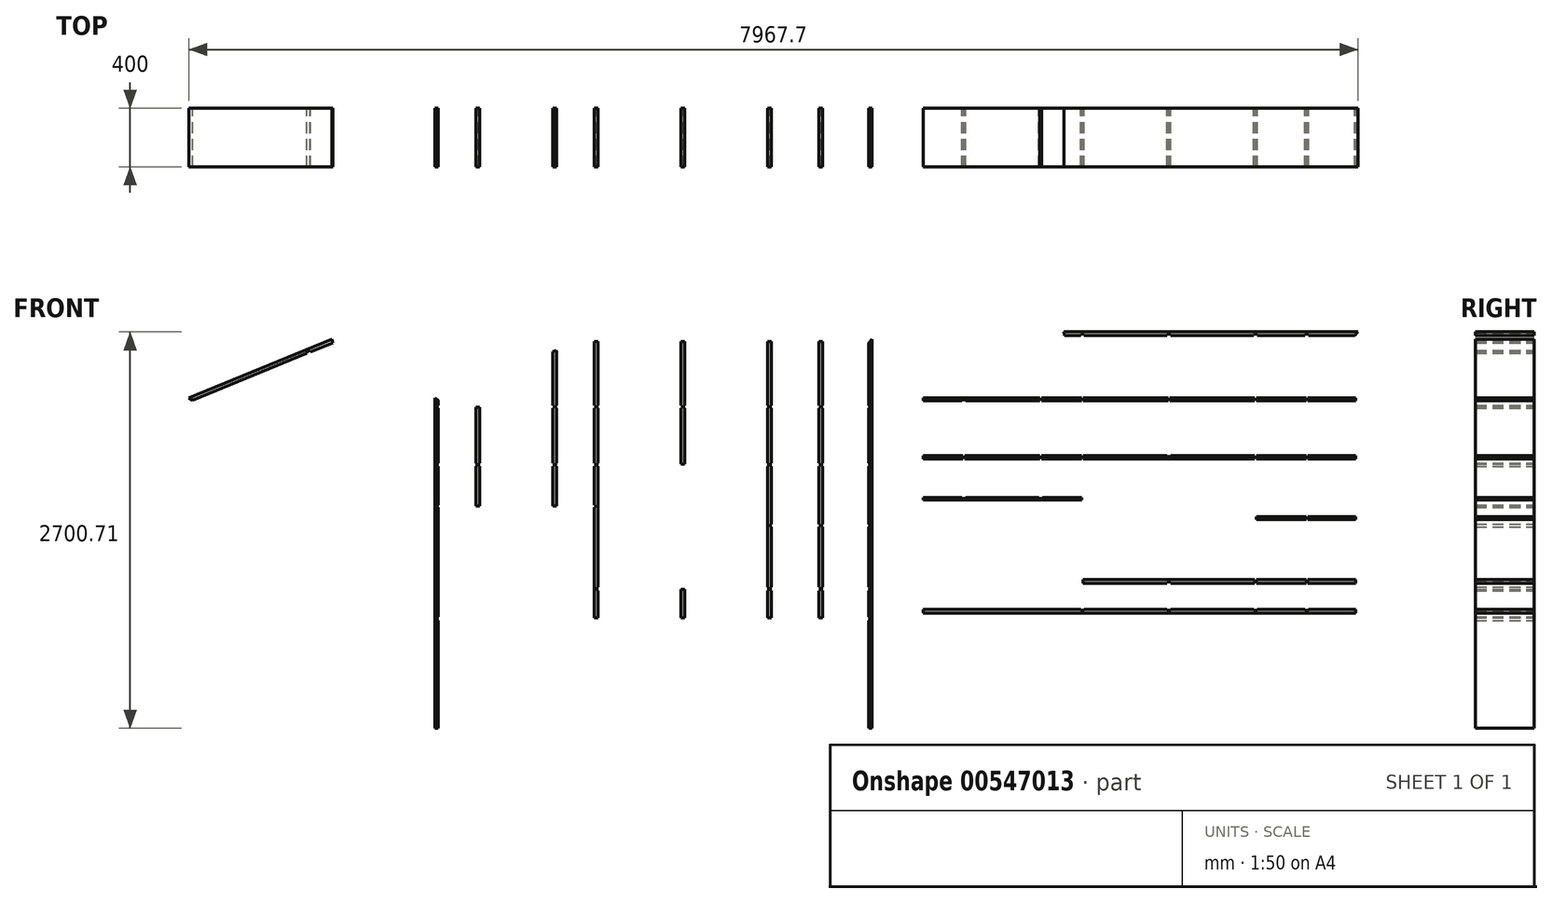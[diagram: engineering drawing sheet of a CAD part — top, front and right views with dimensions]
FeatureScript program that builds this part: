
annotation { "Feature Type Name" : "Feature", "Feature Type Description" : "" }
export const myFeature = defineFeature(function(context is Context, id is Id, definition is map)
    precondition{}
    {
        {
            var Q0;
            Q0=qCreatedBy(makeId("Front.planeOp"),FACE);
            var sketch = newSketch(context, id + "F0", { "sketchPlane" : qUnion([Q0])});
            skLineSegment(sketch, "E0", {"start": v(0, 0) * mm, "end": v(0, 2251) * mm});
            skLineSegment(sketch, "E1", {"start": v(0, 2251) * mm, "end": v(975, 2650) * mm});
            skLineSegment(sketch, "E2", {"start": v(975, 2650) * mm, "end": v(3933.36, 2650) * mm});
            skLineSegment(sketch, "E3", {"start": v(3933.36, 2650) * mm, "end": v(4900, 2240) * mm});
            skLineSegment(sketch, "E4", {"start": v(4900, 2240) * mm, "end": v(4900, 0) * mm});
            skLineSegment(sketch, "E5", {"start": v(4900, 0) * mm, "end": v(0, 0) * mm});
            skLineSegment(sketch, "E6", {"start": v(4550, 0) * mm, "end": v(4550, 2100) * mm});
            skLineSegment(sketch, "E7", {"start": v(4550, 2100) * mm, "end": v(3350, 2100) * mm});
            skLineSegment(sketch, "E8", {"start": v(3350, 2100) * mm, "end": v(3350, 0) * mm});
            skLineSegment(sketch, "E9.bottom", {"start": v(1200, 1695) * mm, "end": v(2180, 1695) * mm});
            skLineSegment(sketch, "E9.top", {"start": v(1200, 1050) * mm, "end": v(2180, 1050) * mm});
            skLineSegment(sketch, "E9.left", {"start": v(1200, 1695) * mm, "end": v(1200, 1050) * mm});
            skLineSegment(sketch, "E9.right", {"start": v(2180, 1695) * mm, "end": v(2180, 1050) * mm});
            skLineSegment(sketch, "E10", {"start": v(2980, 2650) * mm, "end": v(2980, 0) * mm});
            skLineSegment(sketch, "E11.0", {"start": v(24, 0) * mm, "end": v(24, 502) * mm});
            skLineSegment(sketch, "E12.0", {"start": v(2642, 2636) * mm, "end": v(2642, 2626) * mm});
            skLineSegment(sketch, "E13.0", {"start": v(2291.97, 1807) * mm, "end": v(2291.97, 2181) * mm});
            skLineSegment(sketch, "E14.0", {"start": v(2268, 1807) * mm, "end": v(2268, 2181) * mm});
            skLineSegment(sketch, "E15.0", {"start": v(2268, 1783) * mm, "end": v(2268, 962) * mm});
            skLineSegment(sketch, "E16.0", {"start": v(2292, 1783) * mm, "end": v(2292, 1390.5) * mm});
            skLineSegment(sketch, "E17.0", {"start": v(2292, 938) * mm, "end": v(2292, 752) * mm});
            skLineSegment(sketch, "E18.0", {"start": v(2268, 938) * mm, "end": v(2268, 752) * mm});
            skLineSegment(sketch, "E19.0", {"start": v(1702, 1800) * mm, "end": v(1702, 2181) * mm});
            skLineSegment(sketch, "E20.0", {"start": v(1678, 1800) * mm, "end": v(1678, 2181) * mm});
            skLineSegment(sketch, "E21.0", {"start": v(1112, 1807) * mm, "end": v(1112, 2181) * mm});
            skLineSegment(sketch, "E22.0", {"start": v(1088, 1807) * mm, "end": v(1088, 2181) * mm});
            skLineSegment(sketch, "E23.0", {"start": v(1088, 1783) * mm, "end": v(1088, 1522.2) * mm});
            skLineSegment(sketch, "E24.0", {"start": v(1112, 1783) * mm, "end": v(1112, 1222.6) * mm});
            skLineSegment(sketch, "E25.0", {"start": v(1088, 938) * mm, "end": v(1088, 752) * mm});
            skLineSegment(sketch, "E26.0", {"start": v(1112, 938) * mm, "end": v(1112, 752) * mm});
            skLineSegment(sketch, "E27.0", {"start": v(1105, 1783) * mm, "end": v(2275, 1783) * mm});
            skLineSegment(sketch, "E28.0", {"start": v(1105, 1807) * mm, "end": v(1678, 1807) * mm});
            skLineSegment(sketch, "E29.0", {"start": v(1105, 938) * mm, "end": v(1678, 938) * mm});
            skLineSegment(sketch, "E30.0", {"start": v(1105, 962) * mm, "end": v(2275, 962) * mm});
            skLineSegment(sketch, "E31.0", {"start": v(1095, 1807) * mm, "end": v(821.64, 1807) * mm});
            skLineSegment(sketch, "E32.0", {"start": v(1095, 1783) * mm, "end": v(821.64, 1783) * mm});
            skLineSegment(sketch, "E33.0", {"start": v(2284.97, 938) * mm, "end": v(2625, 938) * mm});
            skLineSegment(sketch, "E34.0", {"start": v(2284.97, 962) * mm, "end": v(2625, 962) * mm});
            skLineSegment(sketch, "E35.0", {"start": v(2284.97, 1783) * mm, "end": v(2625, 1783) * mm});
            skLineSegment(sketch, "E36.0", {"start": v(2284.97, 1807) * mm, "end": v(2625, 1807) * mm});
            skLineSegment(sketch, "E37.0", {"start": v(1678, 945) * mm, "end": v(1678, 752) * mm});
            skLineSegment(sketch, "E38.0", {"start": v(1702, 945) * mm, "end": v(1702, 752) * mm});
            skLineSegment(sketch, "E39.0", {"start": v(1095, 1522.2) * mm, "end": v(828.64, 1522.2) * mm});
            skLineSegment(sketch, "E40.0", {"start": v(1095, 1504.2) * mm, "end": v(1088, 1504.2) * mm});
            skLineSegment(sketch, "E41.0", {"start": v(2963, 759) * mm, "end": v(2642, 759) * mm});
            skLineSegment(sketch, "E42", {"start": v(1112, 1222.6) * mm, "end": v(1112, 962) * mm});
            skLineSegment(sketch, "E43.bottom", {"start": v(100, 0) * mm, "end": v(500, 0) * mm});
            skLineSegment(sketch, "E43.left", {"start": v(100, 0) * mm, "end": v(100, 450) * mm});
            skLineSegment(sketch, "E43.right", {"start": v(500, 0) * mm, "end": v(500, 450) * mm});
            skLineSegment(sketch, "E44.bottom", {"start": v(576, 0) * mm, "end": v(976, 0) * mm});
            skLineSegment(sketch, "E44.left", {"start": v(576, 0) * mm, "end": v(576, 450) * mm});
            skLineSegment(sketch, "E44.right", {"start": v(976, 0) * mm, "end": v(976, 450) * mm});
            skLineSegment(sketch, "E45.bottom", {"start": v(1052, 0) * mm, "end": v(1452, 0) * mm});
            skLineSegment(sketch, "E45.left", {"start": v(1052, 0) * mm, "end": v(1052, 650) * mm});
            skLineSegment(sketch, "E45.right", {"start": v(1452, 0) * mm, "end": v(1452, 650) * mm});
            skLineSegment(sketch, "E46.bottom", {"start": v(1528, 0) * mm, "end": v(1928, 0) * mm});
            skLineSegment(sketch, "E46.left", {"start": v(1528, 0) * mm, "end": v(1528, 650) * mm});
            skLineSegment(sketch, "E46.right", {"start": v(1928, 0) * mm, "end": v(1928, 650) * mm});
            skLineSegment(sketch, "E47.bottom", {"start": v(2004, -2.2) * mm, "end": v(2404, -2.2) * mm});
            skLineSegment(sketch, "E47.left", {"start": v(2004, 447.8) * mm, "end": v(2004, 650) * mm});
            skLineSegment(sketch, "E47.right", {"start": v(2404, 447.8) * mm, "end": v(2404, 650) * mm});
            skLineSegment(sketch, "E48.bottom", {"start": v(2450, 0) * mm, "end": v(2850, 0) * mm});
            skLineSegment(sketch, "E49.bottom", {"start": v(2480, 0) * mm, "end": v(2880, 0) * mm});
            skLineSegment(sketch, "E49.left", {"start": v(2480, 0) * mm, "end": v(2480, 650) * mm});
            skLineSegment(sketch, "E49.right", {"start": v(2880, 0) * mm, "end": v(2880, 650) * mm});
            skLineSegment(sketch, "E50", {"start": v(2642, 2636) * mm, "end": v(2618, 2636) * mm});
            skLineSegment(sketch, "E51.trimOffspring", {"start": v(2642, 2626) * mm, "end": v(2956, 2626) * mm});
            skLineSegment(sketch, "E52.trimOffspring", {"start": v(2956, 2249) * mm, "end": v(2956, 2199) * mm});
            skLineSegment(sketch, "E53.trimOffspring", {"start": v(2618, 2249) * mm, "end": v(2618, 2199) * mm});
            skLineSegment(sketch, "E54.trimOffspring", {"start": v(2642, 2249) * mm, "end": v(2642, 2199) * mm});
            skLineSegment(sketch, "E55", {"start": v(1112, 2636) * mm, "end": v(1088, 2636) * mm});
            skLineSegment(sketch, "E56.trimOffspring", {"start": v(1112, 2626) * mm, "end": v(1678, 2626) * mm});
            skLineSegment(sketch, "E57", {"start": v(1702, 2636) * mm, "end": v(1678, 2636) * mm});
            skLineSegment(sketch, "E58.trimOffspring", {"start": v(1702, 2626) * mm, "end": v(2268, 2626) * mm});
            skLineSegment(sketch, "E59", {"start": v(2291.97, 2636) * mm, "end": v(2268, 2636) * mm});
            skLineSegment(sketch, "E60.trimOffspring", {"start": v(2291.97, 2626) * mm, "end": v(2618, 2626) * mm});
            skLineSegment(sketch, "E61", {"start": v(17, 1807) * mm, "end": v(17, 1783) * mm});
            skLineSegment(sketch, "E62.trimOffspring", {"start": v(24, 759) * mm, "end": v(24, 1504.2) * mm});
            skLineSegment(sketch, "E63.trimOffspring", {"start": v(17, 1522.2) * mm, "end": v(17, 1504.2) * mm});
            skLineSegment(sketch, "E64.trimOffspring", {"start": v(24, 1522.2) * mm, "end": v(24, 1783) * mm});
            skLineSegment(sketch, "E65.trimOffspring", {"start": v(24, 1807) * mm, "end": v(24, 2181) * mm});
            skLineSegment(sketch, "E66.trimOffspring", {"start": v(24, 502) * mm, "end": v(24, 735) * mm});
            skLineSegment(sketch, "E67", {"start": v(2963, 1807) * mm, "end": v(2963, 1783) * mm});
            skLineSegment(sketch, "E68.trimOffspring", {"start": v(2963, 1390.5) * mm, "end": v(2963, 1372.5) * mm});
            skLineSegment(sketch, "E69.trimOffspring", {"start": v(2956, 938) * mm, "end": v(2956, 759) * mm});
            skLineSegment(sketch, "E70.trimOffspring", {"start": v(2956, 1783) * mm, "end": v(2956, 1390.5) * mm});
            skLineSegment(sketch, "E71.trimOffspring", {"start": v(2818.11, 1783) * mm, "end": v(2963, 1783) * mm});
            skLineSegment(sketch, "E72", {"start": v(2635, 1807) * mm, "end": v(2635, 1783) * mm});
            skLineSegment(sketch, "E73.trimOffspring", {"start": v(2635, 938) * mm, "end": v(2963, 938) * mm});
            skLineSegment(sketch, "E74.trimOffspring", {"start": v(2642, 938) * mm, "end": v(2642, 752) * mm});
            skLineSegment(sketch, "E75.trimOffspring", {"start": v(2635, 962) * mm, "end": v(2818.11, 962) * mm});
            skLineSegment(sketch, "E76.trimOffspring", {"start": v(2635, 1390.5) * mm, "end": v(2635, 1372.5) * mm});
            skLineSegment(sketch, "E77.trimOffspring", {"start": v(2635, 1807) * mm, "end": v(2963, 1807) * mm});
            skLineSegment(sketch, "E78.trimOffspring", {"start": v(2635, 1783) * mm, "end": v(2818.11, 1783) * mm});
            skLineSegment(sketch, "E79.trimOffspring", {"start": v(2642, 1783) * mm, "end": v(2642, 1390.5) * mm});
            skLineSegment(sketch, "E80", {"start": v(2625, 1807) * mm, "end": v(2625, 1783) * mm});
            skLineSegment(sketch, "E81.trimOffspring", {"start": v(2625, 1390.5) * mm, "end": v(2625, 1372.5) * mm});
            skLineSegment(sketch, "E82.trimOffspring", {"start": v(2618, 1783) * mm, "end": v(2618, 1390.5) * mm});
            skLineSegment(sketch, "E83.trimOffspring", {"start": v(2618, 938) * mm, "end": v(2618, 752) * mm});
            skLineSegment(sketch, "E84.trimOffspring", {"start": v(2818.11, 962) * mm, "end": v(2963, 962) * mm});
            skLineSegment(sketch, "E85", {"start": v(1702, 1800) * mm, "end": v(1678, 1800) * mm});
            skLineSegment(sketch, "E86.trimOffspring", {"start": v(1702, 1807) * mm, "end": v(2275, 1807) * mm});
            skLineSegment(sketch, "E87.trimOffspring", {"start": v(2284.97, 1807) * mm, "end": v(2284.97, 1783) * mm});
            skLineSegment(sketch, "E88.trimOffspring", {"start": v(2284.97, 1390.5) * mm, "end": v(2284.97, 1372.5) * mm});
            skLineSegment(sketch, "E89.trimOffspring", {"start": v(2275, 1783) * mm, "end": v(2275, 1807) * mm});
            skLineSegment(sketch, "E90.trimOffspring", {"start": v(2275, 938) * mm, "end": v(2275, 962) * mm});
            skLineSegment(sketch, "E91.trimOffspring", {"start": v(2956, 502) * mm, "end": v(2956, 0) * mm});
            skLineSegment(sketch, "E92.trimOffspring", {"start": v(1678, 759) * mm, "end": v(1112, 759) * mm});
            skLineSegment(sketch, "E93", {"start": v(1702, 945) * mm, "end": v(1678, 945) * mm});
            skLineSegment(sketch, "E94.trimOffspring", {"start": v(1702, 938) * mm, "end": v(2275, 938) * mm});
            skLineSegment(sketch, "E95.trimOffspring", {"start": v(287.5, 1807) * mm, "end": v(287.5, 1783) * mm});
            skLineSegment(sketch, "E96.trimOffspring", {"start": v(287.5, 1807) * mm, "end": v(17, 1807) * mm});
            skLineSegment(sketch, "E97.trimOffspring", {"start": v(280.5, 1807) * mm, "end": v(280.5, 2188) * mm});
            skLineSegment(sketch, "E98.trimOffspring", {"start": v(304.5, 1807) * mm, "end": v(304.5, 2188) * mm});
            skLineSegment(sketch, "E99.trimOffspring", {"start": v(287.5, 1783) * mm, "end": v(17, 1783) * mm});
            skLineSegment(sketch, "E100.trimOffspring", {"start": v(297.5, 1783) * mm, "end": v(297.5, 1807) * mm});
            skLineSegment(sketch, "E101.trimOffspring", {"start": v(280.5, 1522.2) * mm, "end": v(17, 1522.2) * mm});
            skLineSegment(sketch, "E102.trimOffspring", {"start": v(24, 1504.2) * mm, "end": v(17, 1504.2) * mm});
            skLineSegment(sketch, "E103.trimOffspring", {"start": v(304.5, 1515.2) * mm, "end": v(304.5, 1783) * mm});
            skLineSegment(sketch, "E104.trimOffspring", {"start": v(828.64, 2564.17) * mm, "end": v(828.64, 2249) * mm});
            skLineSegment(sketch, "E105.trimOffspring", {"start": v(804.64, 2565.16) * mm, "end": v(804.64, 2249) * mm});
            skLineSegment(sketch, "E106.trimOffspring", {"start": v(804.64, 1783) * mm, "end": v(804.64, 1515.2) * mm});
            skLineSegment(sketch, "E107.trimOffspring", {"start": v(828.64, 1783) * mm, "end": v(828.64, 1515.2) * mm});
            skLineSegment(sketch, "E108.trimOffspring", {"start": v(811.64, 1783) * mm, "end": v(297.5, 1783) * mm});
            skLineSegment(sketch, "E109.trimOffspring", {"start": v(811.64, 1807) * mm, "end": v(297.5, 1807) * mm});
            skLineSegment(sketch, "E110", {"start": v(1105, 1807) * mm, "end": v(1105, 1783) * mm});
            skLineSegment(sketch, "E111.trimOffspring", {"start": v(1095, 1807) * mm, "end": v(1095, 1783) * mm});
            skLineSegment(sketch, "E112.trimOffspring", {"start": v(1095, 1522.2) * mm, "end": v(1095, 1504.2) * mm});
            skLineSegment(sketch, "E113.trimOffspring", {"start": v(1088, 1504.2) * mm, "end": v(1088, 1222.6) * mm});
            skLineSegment(sketch, "E114.trimOffspring", {"start": v(1088, 1222.6) * mm, "end": v(1088, 938) * mm});
            skLineSegment(sketch, "E115", {"start": v(1105, 962) * mm, "end": v(1105, 938) * mm});
            skLineSegment(sketch, "E116.trimOffspring", {"start": v(280.5, 1515.2) * mm, "end": v(280.5, 1783) * mm});
            skLineSegment(sketch, "E117", {"start": v(304.5, 1522.2) * mm, "end": v(804.64, 1522.2) * mm});
            skLineSegment(sketch, "E118.0", {"start": v(576, 650) * mm, "end": v(976, 650) * mm});
            skLineSegment(sketch, "E119.0", {"start": v(100, 650) * mm, "end": v(500, 650) * mm});
            skLineSegment(sketch, "E120", {"start": v(500, 650) * mm, "end": v(500, 450) * mm});
            skLineSegment(sketch, "E121", {"start": v(100, 650) * mm, "end": v(100, 450) * mm});
            skLineSegment(sketch, "E122", {"start": v(576, 650) * mm, "end": v(576, 450) * mm});
            skLineSegment(sketch, "E123", {"start": v(976, 650) * mm, "end": v(976, 450) * mm});
            skLineSegment(sketch, "E124", {"start": v(2284.97, 1372.5) * mm, "end": v(2625, 1372.5) * mm});
            skLineSegment(sketch, "E125.0", {"start": v(2284.97, 1390.5) * mm, "end": v(2625, 1390.5) * mm});
            skPoint(sketch, "E126.orphan", {"position": v(2292, 1372.5) * mm});
            skLineSegment(sketch, "E127.trimOffspring", {"start": v(2292, 1372.5) * mm, "end": v(2292, 962) * mm});
            skLineSegment(sketch, "E128.trimOffspring", {"start": v(2284.97, 962) * mm, "end": v(2284.97, 938) * mm});
            skPoint(sketch, "E129.orphan", {"position": v(2956, 1372.5) * mm});
            skLineSegment(sketch, "E130.trimOffspring", {"start": v(2956, 1372.5) * mm, "end": v(2956, 962) * mm});
            skLineSegment(sketch, "E131.trimOffspring", {"start": v(2963, 962) * mm, "end": v(2963, 938) * mm});
            skLineSegment(sketch, "E132", {"start": v(2625, 962) * mm, "end": v(2625, 938) * mm});
            skLineSegment(sketch, "E133", {"start": v(2635, 962) * mm, "end": v(2635, 938) * mm});
            skLineSegment(sketch, "E134.trimOffspring", {"start": v(2642, 1372.5) * mm, "end": v(2642, 962) * mm});
            skLineSegment(sketch, "E135.trimOffspring", {"start": v(2618, 1372.5) * mm, "end": v(2618, 962) * mm});
            skLineSegment(sketch, "E136.trimOffspring", {"start": v(2635, 1372.5) * mm, "end": v(2963, 1372.5) * mm});
            skLineSegment(sketch, "E137.trimOffspring", {"start": v(2635, 1390.5) * mm, "end": v(2963, 1390.5) * mm});
            skLineSegment(sketch, "E138.trimOffspring", {"start": v(804.64, 2249) * mm, "end": v(804.64, 2199) * mm});
            skLineSegment(sketch, "E139.trimOffspring", {"start": v(828.64, 2249) * mm, "end": v(828.64, 2199) * mm});
            skLineSegment(sketch, "E140.trimOffspring", {"start": v(828.64, 2564.17) * mm, "end": v(979.72, 2626) * mm});
            skLineSegment(sketch, "E141.trimOffspring", {"start": v(804.64, 2565.16) * mm, "end": v(824.85, 2573.43) * mm});
            skLineSegment(sketch, "E142", {"start": v(1088, 2636) * mm, "end": v(1088, 2249) * mm});
            skLineSegment(sketch, "E143", {"start": v(1112, 2636) * mm, "end": v(1112, 2249) * mm});
            skLineSegment(sketch, "E144", {"start": v(1678, 2249) * mm, "end": v(1678, 2636) * mm});
            skLineSegment(sketch, "E145", {"start": v(1702, 2636) * mm, "end": v(1702, 2249) * mm});
            skLineSegment(sketch, "E146", {"start": v(2268, 2636) * mm, "end": v(2268, 2249) * mm});
            skLineSegment(sketch, "E147", {"start": v(2291.97, 2249) * mm, "end": v(2291.97, 2636) * mm});
            skLineSegment(sketch, "E148", {"start": v(2618, 2636) * mm, "end": v(2618, 2249) * mm});
            skLineSegment(sketch, "E149", {"start": v(2642, 2626) * mm, "end": v(2642, 2249) * mm});
            skLineSegment(sketch, "E150", {"start": v(2956, 2626) * mm, "end": v(2956, 2249) * mm});
            skLineSegment(sketch, "E151.trimOffspring", {"start": v(1088, 759) * mm, "end": v(17, 759) * mm});
            skLineSegment(sketch, "E152.0", {"start": v(280.5, 1515.2) * mm, "end": v(304.5, 1515.2) * mm});
            skLineSegment(sketch, "E153.trimOffspring", {"start": v(804.64, 1515.2) * mm, "end": v(828.64, 1515.2) * mm});
            skLineSegment(sketch, "E154", {"start": v(1088, 1504.2) * mm, "end": v(24, 1504.2) * mm});
            skLineSegment(sketch, "E155.trimOffspring", {"start": v(2956, 526) * mm, "end": v(2956, 502) * mm});
            skLineSegment(sketch, "E156", {"start": v(2004, 447.8) * mm, "end": v(2004, -2.2) * mm});
            skLineSegment(sketch, "E157", {"start": v(2404, 447.8) * mm, "end": v(2404, -2.2) * mm});
            skLineSegment(sketch, "E158.trimOffspring", {"start": v(1052, 650) * mm, "end": v(1452, 650) * mm});
            skLineSegment(sketch, "E159.trimOffspring", {"start": v(1528, 650) * mm, "end": v(1928, 650) * mm});
            skLineSegment(sketch, "E160.trimOffspring", {"start": v(2004, 650) * mm, "end": v(2404, 650) * mm});
            skLineSegment(sketch, "E161.trimOffspring", {"start": v(2480, 650) * mm, "end": v(2880, 650) * mm});
            skLineSegment(sketch, "E162", {"start": v(1685, 741) * mm, "end": v(1695, 741) * mm});
            skLineSegment(sketch, "E163", {"start": v(2956, 550) * mm, "end": v(2956, 526) * mm});
            skLineSegment(sketch, "E164.0", {"start": v(2642, 752) * mm, "end": v(2618, 752) * mm});
            skLineSegment(sketch, "E165.trimOffspring", {"start": v(2618, 759) * mm, "end": v(2292, 759) * mm});
            skLineSegment(sketch, "E166.trimOffspring", {"start": v(2268, 759) * mm, "end": v(1702, 759) * mm});
            skLineSegment(sketch, "E167.trimOffspring", {"start": v(2292, 752) * mm, "end": v(2268, 752) * mm});
            skLineSegment(sketch, "E168.trimOffspring", {"start": v(1112, 752) * mm, "end": v(1088, 752) * mm});
            skLineSegment(sketch, "E169.trimOffspring", {"start": v(1702, 752) * mm, "end": v(1678, 752) * mm});
            skLineSegment(sketch, "E170.trimOffspring", {"start": v(2963, 759) * mm, "end": v(2963, 735) * mm});
            skLineSegment(sketch, "E171.trimOffspring", {"start": v(2956, 735) * mm, "end": v(2956, 550) * mm});
            skLineSegment(sketch, "E172", {"start": v(975, 2650) * mm, "end": v(979.72, 2626) * mm});
            skLineSegment(sketch, "E173", {"start": v(17, 2199) * mm, "end": v(17, 2181) * mm});
            skLineSegment(sketch, "E174", {"start": v(17, 2181) * mm, "end": v(24, 2181) * mm});
            skLineSegment(sketch, "E175.0", {"start": v(17, 2181) * mm, "end": v(280.5, 2181) * mm});
            skLineSegment(sketch, "E176.0", {"start": v(17, 2199) * mm, "end": v(298.67, 2199) * mm});
            skLineSegment(sketch, "E177", {"start": v(2963, 2199) * mm, "end": v(2963, 2181) * mm});
            skLineSegment(sketch, "E178", {"start": v(2635, 2199) * mm, "end": v(2635, 2181) * mm});
            skLineSegment(sketch, "E179", {"start": v(2625, 2199) * mm, "end": v(2625, 2181) * mm});
            skLineSegment(sketch, "E180.trimOffspring", {"start": v(2635, 2199) * mm, "end": v(2963, 2199) * mm});
            skLineSegment(sketch, "E181.trimOffspring", {"start": v(2635, 2181) * mm, "end": v(2963, 2181) * mm});
            skLineSegment(sketch, "E182.trimOffspring", {"start": v(2284.97, 2199) * mm, "end": v(2284.97, 2181) * mm});
            skLineSegment(sketch, "E183.trimOffspring", {"start": v(2284.97, 2199) * mm, "end": v(2625, 2199) * mm});
            skLineSegment(sketch, "E184.trimOffspring", {"start": v(2284.97, 2181) * mm, "end": v(2625, 2181) * mm});
            skLineSegment(sketch, "E185.trimOffspring", {"start": v(2275, 2181) * mm, "end": v(2275, 2199) * mm});
            skLineSegment(sketch, "E186", {"start": v(1695, 2199) * mm, "end": v(1695, 2181) * mm});
            skLineSegment(sketch, "E187", {"start": v(1685, 2199) * mm, "end": v(1685, 2181) * mm});
            skLineSegment(sketch, "E188.trimOffspring", {"start": v(1695, 2199) * mm, "end": v(2275, 2199) * mm});
            skLineSegment(sketch, "E189.trimOffspring", {"start": v(1695, 2181) * mm, "end": v(2275, 2181) * mm});
            skLineSegment(sketch, "E190.trimOffspring", {"start": v(298.67, 2199) * mm, "end": v(811.64, 2199) * mm});
            skLineSegment(sketch, "E191.trimOffspring", {"start": v(304.5, 2181) * mm, "end": v(811.64, 2181) * mm});
            skLineSegment(sketch, "E192.trimOffspring", {"start": v(821.64, 2199) * mm, "end": v(1095, 2199) * mm});
            skLineSegment(sketch, "E193.trimOffspring", {"start": v(821.64, 2181) * mm, "end": v(1095, 2181) * mm});
            skLineSegment(sketch, "E194.trimOffspring", {"start": v(811.64, 2199) * mm, "end": v(811.64, 2181) * mm});
            skLineSegment(sketch, "E195", {"start": v(1105, 2199) * mm, "end": v(1105, 2181) * mm});
            skLineSegment(sketch, "E196.trimOffspring", {"start": v(1105, 2199) * mm, "end": v(1685, 2199) * mm});
            skLineSegment(sketch, "E197.trimOffspring", {"start": v(1105, 2181) * mm, "end": v(1685, 2181) * mm});
            skLineSegment(sketch, "E198.trimOffspring", {"start": v(1095, 2199) * mm, "end": v(1095, 2181) * mm});
            skLineSegment(sketch, "E199.trimOffspring", {"start": v(804.64, 2181) * mm, "end": v(804.64, 1807) * mm});
            skLineSegment(sketch, "E200.trimOffspring", {"start": v(828.64, 2181) * mm, "end": v(828.64, 1807) * mm});
            skLineSegment(sketch, "E201.trimOffspring", {"start": v(1088, 2199) * mm, "end": v(1088, 2249) * mm});
            skLineSegment(sketch, "E202.trimOffspring", {"start": v(1112, 2199) * mm, "end": v(1112, 2249) * mm});
            skLineSegment(sketch, "E203.trimOffspring", {"start": v(1678, 2199) * mm, "end": v(1678, 2249) * mm});
            skLineSegment(sketch, "E204.trimOffspring", {"start": v(1702, 2199) * mm, "end": v(1702, 2249) * mm});
            skLineSegment(sketch, "E205.trimOffspring", {"start": v(2268, 2199) * mm, "end": v(2268, 2249) * mm});
            skLineSegment(sketch, "E206.trimOffspring", {"start": v(2291.97, 2199) * mm, "end": v(2291.97, 2249) * mm});
            skLineSegment(sketch, "E207.trimOffspring", {"start": v(2618, 2181) * mm, "end": v(2618, 1807) * mm});
            skLineSegment(sketch, "E208.trimOffspring", {"start": v(2642, 2181) * mm, "end": v(2642, 1807) * mm});
            skLineSegment(sketch, "E209.trimOffspring", {"start": v(2956, 2181) * mm, "end": v(2956, 1807) * mm});
            skLineSegment(sketch, "E210", {"start": v(0, 2251) * mm, "end": v(24, 2234.89) * mm});
            skLineSegment(sketch, "E211.trimOffspring", {"start": v(24, 2199) * mm, "end": v(24, 2234.89) * mm});
            skLineSegment(sketch, "E212", {"start": v(811.64, 1807) * mm, "end": v(811.64, 1783) * mm});
            skLineSegment(sketch, "E213.0", {"start": v(1105, 735) * mm, "end": v(17, 735) * mm});
            skLineSegment(sketch, "E213.1", {"start": v(2963, 735) * mm, "end": v(1105, 735) * mm});
            skLineSegment(sketch, "E214", {"start": v(17, 759) * mm, "end": v(17, 735) * mm});
            skLineSegment(sketch, "E215", {"start": v(828.64, 2564.17) * mm, "end": v(824.85, 2573.43) * mm});
            skLineSegment(sketch, "E216.trimOffspring", {"start": v(979.72, 2626) * mm, "end": v(1088, 2626) * mm});
            skLineSegment(sketch, "E217.trimOffspring", {"start": v(24, 2234.89) * mm, "end": v(804.64, 2554.35) * mm});
            skLineSegment(sketch, "E218", {"start": v(2956, 2626) * mm, "end": v(2980, 2650) * mm});
            skLineSegment(sketch, "E219.0", {"start": v(821.64, 1807) * mm, "end": v(821.64, 1783) * mm});
            skLineSegment(sketch, "E220", {"start": v(821.64, 2199) * mm, "end": v(821.64, 2181) * mm});
            skPoint(sketch, "E221.trimOffspring.start.orphan", {"position": v(822.04, 2181) * mm});
            skLineSegment(sketch, "E222.0", {"start": v(280.5, 2188) * mm, "end": v(304.5, 2188) * mm});
            skSolve(sketch);
        }
        {
            var Q0;
            {var subQ12=sQuery(id+"F0.wireOp",EDGE,"cc0fc2fd-8950-4ce1-810f-629987963abd.0");Q0=makeQuery(id+"F0.imprint","IMPRINT",FACE,{"disambiguationData":[TD([[makeQuery(id+"F0.imprint","IMPRINT",EDGE,{"derivedFrom":subQ12}),1.0]])]});}
            var Q1;
            {var subQ12=sQuery(id+"F0.wireOp",EDGE,"Zqx6Wrpy-ailH-Ofh8-OMIL-Cnyi6wDhXa7h");Q1=makeQuery(id+"F0.imprint","IMPRINT",FACE,{"disambiguationData":[TD([[makeQuery(id+"F0.imprint","IMPRINT",EDGE,{"derivedFrom":subQ12}),-1.0]])]});}
            var Q2;
            {var subQ16=sQuery(id+"F0.wireOp",EDGE,"U11PcNi1-iFkQ-JOyU-lKJq-kTwDv0TLeNX1");Q2=makeQuery(id+"F0.imprint","IMPRINT",FACE,{"disambiguationData":[TD([[makeQuery(id+"F0.imprint","IMPRINT",EDGE,{"derivedFrom":subQ16}),1.0]])]});}
            var Q3;
            {var subQ4=sQuery(id+"F0.wireOp",EDGE,"E11.0");Q3=makeQuery(id+"F0.imprint","IMPRINT",FACE,{"disambiguationData":[TD([[makeQuery(id+"F0.imprint","IMPRINT",EDGE,{"derivedFrom":subQ4}),1.0]])]});}
            var Q4;
            {var subQ3=sQuery(id+"F0.wireOp",EDGE,"E91.trimOffspring");Q4=makeQuery(id+"F0.imprint","IMPRINT",FACE,{"disambiguationData":[TD([[makeQuery(id+"F0.imprint","IMPRINT",EDGE,{"derivedFrom":subQ3}),1.0]])]});}
            var Q5;
            Q5=makeQuery(id+"F0.imprint","IMPRINT",FACE,{"disambiguationData":[TD([[makeQuery(id+"F0.imprint","IMPRINT",EDGE,{"derivedFrom":sQuery(id+"F0.wireOp",EDGE,"1fa08ccf-63a5-4874-b047-1c911d15539b.0")}),1.0]])]});
            var Q6;
            Q6=makeQuery(id+"F0.imprint","IMPRINT",FACE,{"disambiguationData":[TD([[makeQuery(id+"F0.imprint","IMPRINT",EDGE,{"derivedFrom":sQuery(id+"F0.wireOp",EDGE,"E12.0")}),-1.0]])]});
            var Q7;
            {var subQ11=sQuery(id+"F0.wireOp",EDGE,"E13.0");Q7=makeQuery(id+"F0.imprint","IMPRINT",FACE,{"disambiguationData":[TD([[makeQuery(id+"F0.imprint","IMPRINT",EDGE,{"derivedFrom":subQ11}),1.0]])]});}
            var Q8;
            {var subQ8=sQuery(id+"F0.wireOp",EDGE,"723af7a5-55d7-4603-a10d-ee5387bef70e.trimOffspring");Q8=makeQuery(id+"F0.imprint","IMPRINT",FACE,{"disambiguationData":[TD([[makeQuery(id+"F0.imprint","IMPRINT",EDGE,{"derivedFrom":subQ8}),-1.0]])]});}
            var Q9;
            {var subQ13=sQuery(id+"F0.wireOp",EDGE,"j7I8hBcO-UPLF-qasG-mkQ5-tIXsxcX5kJvB");Q9=makeQuery(id+"F0.imprint","IMPRINT",FACE,{"disambiguationData":[TD([[makeQuery(id+"F0.imprint","IMPRINT",EDGE,{"derivedFrom":subQ13}),-1.0]])]});}
            var Q10;
            {var subQ9=sQuery(id+"F0.wireOp",EDGE,"1c1e2532-dafd-4da4-a65b-c81576773872.trimOffspring");Q10=makeQuery(id+"F0.imprint","IMPRINT",FACE,{"disambiguationData":[TD([[makeQuery(id+"F0.imprint","IMPRINT",EDGE,{"derivedFrom":subQ9}),-1.0]])]});}
            var Q11;
            Q11=makeQuery(id+"F0.imprint","IMPRINT",FACE,{"disambiguationData":[TD([[makeQuery(id+"F0.imprint","IMPRINT",EDGE,{"derivedFrom":sQuery(id+"F0.wireOp",EDGE,"E49.top")}),-1.0]])]});
            var Q12;
            {var subQ5=sQuery(id+"F0.wireOp",EDGE,"E47.top");Q12=makeQuery(id+"F0.imprint","IMPRINT",FACE,{"disambiguationData":[TD([[makeQuery(id+"F0.imprint","IMPRINT",EDGE,{"derivedFrom":subQ5}),-1.0]])]});}
            var Q13;
            {var subQ4=sQuery(id+"F0.wireOp",EDGE,"gVer7gKP-26y5-2fMp-I08D-EYUUCLNE8SVg");Q13=makeQuery(id+"F0.imprint","IMPRINT",FACE,{"disambiguationData":[TD([[makeQuery(id+"F0.imprint","IMPRINT",EDGE,{"derivedFrom":subQ4}),-1.0]])]});}
            var Q14;
            {var subQ0=sQuery(id+"F0.wireOp",EDGE,"yVwcw5Hs-JsNZ-hhUT-rfuA-YBKRWfY8OPYi");Q14=makeQuery(id+"F0.imprint","IMPRINT",FACE,{"disambiguationData":[TD([[makeQuery(id+"F0.imprint","IMPRINT",EDGE,{"derivedFrom":subQ0}),1.0]])]});}
            var Q15;
            {var subQ4=sQuery(id+"F0.wireOp",EDGE,"FRYiaQcv-jFTv-ZeIX-rVMD-ZOG7lv2GNb6S");Q15=makeQuery(id+"F0.imprint","IMPRINT",FACE,{"disambiguationData":[TD([[makeQuery(id+"F0.imprint","IMPRINT",EDGE,{"derivedFrom":subQ4}),-1.0]])]});}
            var Q16;
            {var subQ11=sQuery(id+"F0.wireOp",EDGE,"7499d183-20a8-4fbd-b7f9-f0c2cceccf57.trimOffspring");Q16=makeQuery(id+"F0.imprint","IMPRINT",FACE,{"disambiguationData":[TD([[makeQuery(id+"F0.imprint","IMPRINT",EDGE,{"derivedFrom":subQ11}),1.0]])]});}
            var Q17;
            {var subQ6=sQuery(id+"F0.wireOp",EDGE,"4uqoLxak-8dQo-QfdN-CZMn-XK6vGcTCFNYD");Q17=makeQuery(id+"F0.imprint","IMPRINT",FACE,{"disambiguationData":[TD([[makeQuery(id+"F0.imprint","IMPRINT",EDGE,{"derivedFrom":subQ6}),1.0]])]});}
            var Q18;
            {var subQ1=sQuery(id+"F0.wireOp",EDGE,"E95.trimOffspring");Q18=makeQuery(id+"F0.imprint","IMPRINT",FACE,{"disambiguationData":[TD([[makeQuery(id+"F0.imprint","IMPRINT",EDGE,{"derivedFrom":subQ1}),1.0]])]});}
            var Q19;
            {var subQ11=sQuery(id+"F0.wireOp",EDGE,"7cb3f377-9cc4-4310-baef-f53347c5b779.trimOffspring");Q19=makeQuery(id+"F0.imprint","IMPRINT",FACE,{"disambiguationData":[TD([[makeQuery(id+"F0.imprint","IMPRINT",EDGE,{"derivedFrom":subQ11}),-1.0]])]});}
            var Q20;
            {var subQ20=sQuery(id+"F0.wireOp",EDGE,"E21.0");Q20=makeQuery(id+"F0.imprint","IMPRINT",FACE,{"disambiguationData":[TD([[makeQuery(id+"F0.imprint","IMPRINT",EDGE,{"derivedFrom":subQ20}),1.0]])]});}
            var Q21;
            {var subQ4=sQuery(id+"F0.wireOp",EDGE,"E93");Q21=makeQuery(id+"F0.imprint","IMPRINT",FACE,{"disambiguationData":[TD([[makeQuery(id+"F0.imprint","IMPRINT",EDGE,{"derivedFrom":subQ4}),1.0]])]});}
            var Q22;
            {var subQ0=sQuery(id+"F0.wireOp",EDGE,"E41.0");var subQ1=sQuery(id+"F0.wireOp",EDGE,"E10");var subQ2=makeQuery(id+"F0.imprint","INTERSECT",VERTEX,{"derivedFrom":[subQ1,subQ0]});Q22=makeQuery(id+"F0.imprint","IMPRINT",FACE,{"disambiguationData":[TD([[makeQuery(id+"F0.imprint","IMPRINT",EDGE,{"disambiguationData":[TD([[subQ2,-1.0]])],"derivedFrom":subQ1}),-1.0]])]});}
            var Q23;
            {var subQ0=sQuery(id+"F0.wireOp",EDGE,"E74.trimOffspring");var subQ1=sQuery(id+"F0.wireOp",EDGE,"E41.0");var subQ2=makeQuery(id+"F0.imprint","INTERSECT",VERTEX,{"derivedFrom":[subQ1,subQ0]});Q23=makeQuery(id+"F0.imprint","IMPRINT",FACE,{"disambiguationData":[TD([[makeQuery(id+"F0.imprint","IMPRINT",EDGE,{"disambiguationData":[TD([[subQ2,-1.0]])],"derivedFrom":subQ1}),1.0]])]});}
            var Q24;
            {var subQ5=sQuery(id+"F0.wireOp",EDGE,"yVwcw5Hs-JsNZ-hhUT-rfuA-YBKRWfY8OPYi");Q24=makeQuery(id+"F0.imprint","IMPRINT",FACE,{"disambiguationData":[TD([[makeQuery(id+"F0.imprint","IMPRINT",EDGE,{"derivedFrom":subQ5}),-1.0]])]});}
            var Q25;
            {var subQ4=sQuery(id+"F0.wireOp",EDGE,"E57");Q25=makeQuery(id+"F0.imprint","IMPRINT",FACE,{"disambiguationData":[TD([[makeQuery(id+"F0.imprint","IMPRINT",EDGE,{"derivedFrom":subQ4}),1.0]])]});}
            var Q26;
            {var subQ8=sQuery(id+"F0.wireOp",EDGE,"033eae94-69e5-4012-ae8d-a5502aea84b5.trimOffspring");Q26=makeQuery(id+"F0.imprint","IMPRINT",FACE,{"disambiguationData":[TD([[makeQuery(id+"F0.imprint","IMPRINT",EDGE,{"derivedFrom":subQ8}),1.0]])]});}
            var Q27;
            Q27=makeQuery(id+"F0.imprint","IMPRINT",FACE,{"disambiguationData":[TD([[makeQuery(id+"F0.imprint","IMPRINT",EDGE,{"derivedFrom":sQuery(id+"F0.wireOp",EDGE,"E104.trimOffspring")}),-1.0]])]});
            extrude(context, id + "F1", {"entities" : qUnion([Q0, Q1, Q2, Q3, Q4, Q5, Q6, Q7, Q8, Q9, Q10, Q11, Q12, Q13, Q14, Q15, Q16, Q17, Q18, Q19, Q20, Q21, Q22, Q23, Q24, Q25, Q26, Q27]), "depth" : 400 * mm, "offsetDistance" : 25 * mm});
        }
        {
            var Q0;
            Q0=qCreatedBy(makeId("Front.planeOp"),FACE);
            var sketch = newSketch(context, id + "F2", { "sketchPlane" : qUnion([Q0])});
            skLineSegment(sketch, "E223", {"start": v(3311.66, 50.71) * mm, "end": v(3311.66, 2301.71) * mm});
            skLineSegment(sketch, "E224", {"start": v(3311.66, 2301.71) * mm, "end": v(4286.66, 2700.71) * mm});
            skLineSegment(sketch, "E225", {"start": v(4286.66, 2700.71) * mm, "end": v(7245.01, 2700.71) * mm});
            skLineSegment(sketch, "E226", {"start": v(7245.01, 2700.71) * mm, "end": v(8211.66, 2290.71) * mm});
            skLineSegment(sketch, "E227", {"start": v(8211.66, 2290.71) * mm, "end": v(8211.66, 50.71) * mm});
            skLineSegment(sketch, "E228", {"start": v(8211.66, 50.71) * mm, "end": v(3311.66, 50.71) * mm});
            skLineSegment(sketch, "E229", {"start": v(7861.66, 50.71) * mm, "end": v(7861.66, 2150.71) * mm});
            skLineSegment(sketch, "E230", {"start": v(7861.66, 2150.71) * mm, "end": v(6661.66, 2150.71) * mm});
            skLineSegment(sketch, "E231", {"start": v(6661.66, 2150.71) * mm, "end": v(6661.66, 50.71) * mm});
            skLineSegment(sketch, "E232.bottom", {"start": v(4511.66, 1745.71) * mm, "end": v(5491.66, 1745.71) * mm});
            skLineSegment(sketch, "E232.top", {"start": v(4511.66, 1100.71) * mm, "end": v(5491.66, 1100.71) * mm});
            skLineSegment(sketch, "E232.left", {"start": v(4511.66, 1745.71) * mm, "end": v(4511.66, 1100.71) * mm});
            skLineSegment(sketch, "E232.right", {"start": v(5491.66, 1745.71) * mm, "end": v(5491.66, 1100.71) * mm});
            skLineSegment(sketch, "E233", {"start": v(6291.66, 2700.71) * mm, "end": v(6291.66, 50.71) * mm});
            skLineSegment(sketch, "E234.0", {"start": v(3335.66, 50.71) * mm, "end": v(3335.66, 552.71) * mm});
            skLineSegment(sketch, "E235.0", {"start": v(4291.38, 2676.71) * mm, "end": v(4399.66, 2676.71) * mm});
            skLineSegment(sketch, "E236.0", {"start": v(5953.66, 2686.71) * mm, "end": v(5953.66, 2676.71) * mm});
            skLineSegment(sketch, "E237.0", {"start": v(5603.63, 1857.71) * mm, "end": v(5603.63, 2231.71) * mm});
            skLineSegment(sketch, "E238.0", {"start": v(5579.66, 1857.71) * mm, "end": v(5579.66, 2231.71) * mm});
            skLineSegment(sketch, "E239.0", {"start": v(5579.66, 1833.71) * mm, "end": v(5579.66, 1012.71) * mm});
            skLineSegment(sketch, "E240.0", {"start": v(5603.66, 1833.71) * mm, "end": v(5603.66, 1441.21) * mm});
            skLineSegment(sketch, "E241.0", {"start": v(5603.66, 988.71) * mm, "end": v(5603.66, 802.71) * mm});
            skLineSegment(sketch, "E242.0", {"start": v(5579.66, 988.71) * mm, "end": v(5579.66, 802.71) * mm});
            skLineSegment(sketch, "E243.0", {"start": v(5013.66, 1850.71) * mm, "end": v(5013.66, 2231.71) * mm});
            skLineSegment(sketch, "E244.0", {"start": v(4989.66, 1850.71) * mm, "end": v(4989.66, 2231.71) * mm});
            skLineSegment(sketch, "E245.0", {"start": v(4423.66, 1857.71) * mm, "end": v(4423.66, 2231.71) * mm});
            skLineSegment(sketch, "E246.0", {"start": v(4399.66, 1857.71) * mm, "end": v(4399.66, 2231.71) * mm});
            skLineSegment(sketch, "E247.0", {"start": v(4399.66, 1833.71) * mm, "end": v(4399.66, 1572.91) * mm});
            skLineSegment(sketch, "E248.0", {"start": v(4423.66, 1833.71) * mm, "end": v(4423.66, 1273.31) * mm});
            skLineSegment(sketch, "E249.0", {"start": v(4399.66, 988.71) * mm, "end": v(4399.66, 802.71) * mm});
            skLineSegment(sketch, "E250.0", {"start": v(4423.66, 988.71) * mm, "end": v(4423.66, 802.71) * mm});
            skLineSegment(sketch, "E251.0", {"start": v(4416.66, 1833.71) * mm, "end": v(5586.66, 1833.71) * mm});
            skLineSegment(sketch, "E252.0", {"start": v(4416.66, 1857.71) * mm, "end": v(4989.66, 1857.71) * mm});
            skLineSegment(sketch, "E253.0", {"start": v(4416.66, 988.71) * mm, "end": v(4989.66, 988.71) * mm});
            skLineSegment(sketch, "E254.0", {"start": v(4416.66, 1012.71) * mm, "end": v(5586.66, 1012.71) * mm});
            skLineSegment(sketch, "E255.0", {"start": v(4406.66, 1857.71) * mm, "end": v(4133.3, 1857.71) * mm});
            skLineSegment(sketch, "E256.0", {"start": v(4406.66, 1833.71) * mm, "end": v(4133.3, 1833.71) * mm});
            skLineSegment(sketch, "E257.0", {"start": v(5596.63, 988.71) * mm, "end": v(5936.66, 988.71) * mm});
            skLineSegment(sketch, "E258.0", {"start": v(5596.63, 1012.71) * mm, "end": v(5936.66, 1012.71) * mm});
            skLineSegment(sketch, "E259.0", {"start": v(5596.63, 1833.71) * mm, "end": v(5936.66, 1833.71) * mm});
            skLineSegment(sketch, "E260.0", {"start": v(5596.63, 1857.71) * mm, "end": v(5936.66, 1857.71) * mm});
            skLineSegment(sketch, "E261.0", {"start": v(4989.66, 995.71) * mm, "end": v(4989.66, 802.71) * mm});
            skLineSegment(sketch, "E262.0", {"start": v(5013.66, 995.71) * mm, "end": v(5013.66, 802.71) * mm});
            skLineSegment(sketch, "E263.0", {"start": v(4406.66, 1572.91) * mm, "end": v(4140.3, 1572.91) * mm});
            skLineSegment(sketch, "E264.0", {"start": v(4406.66, 1554.91) * mm, "end": v(4399.66, 1554.91) * mm});
            skLineSegment(sketch, "E265.0", {"start": v(6274.66, 809.71) * mm, "end": v(5953.66, 809.71) * mm});
            skLineSegment(sketch, "E266", {"start": v(4423.66, 1273.31) * mm, "end": v(4423.66, 1012.71) * mm});
            skLineSegment(sketch, "E267.bottom", {"start": v(3411.66, 50.71) * mm, "end": v(3811.66, 50.71) * mm});
            skLineSegment(sketch, "E267.left", {"start": v(3411.66, 50.71) * mm, "end": v(3411.66, 500.71) * mm});
            skLineSegment(sketch, "E267.right", {"start": v(3811.66, 50.71) * mm, "end": v(3811.66, 500.71) * mm});
            skLineSegment(sketch, "E268.bottom", {"start": v(3887.66, 50.71) * mm, "end": v(4287.66, 50.71) * mm});
            skLineSegment(sketch, "E268.left", {"start": v(3887.66, 50.71) * mm, "end": v(3887.66, 500.71) * mm});
            skLineSegment(sketch, "E268.right", {"start": v(4287.66, 50.71) * mm, "end": v(4287.66, 500.71) * mm});
            skLineSegment(sketch, "E269.bottom", {"start": v(4363.66, 50.71) * mm, "end": v(4763.66, 50.71) * mm});
            skLineSegment(sketch, "E269.left", {"start": v(4363.66, 50.71) * mm, "end": v(4363.66, 700.71) * mm});
            skLineSegment(sketch, "E269.right", {"start": v(4763.66, 50.71) * mm, "end": v(4763.66, 700.71) * mm});
            skLineSegment(sketch, "E270.bottom", {"start": v(4839.66, 50.71) * mm, "end": v(5239.66, 50.71) * mm});
            skLineSegment(sketch, "E270.left", {"start": v(4839.66, 50.71) * mm, "end": v(4839.66, 700.71) * mm});
            skLineSegment(sketch, "E270.right", {"start": v(5239.66, 50.71) * mm, "end": v(5239.66, 700.71) * mm});
            skLineSegment(sketch, "E271.bottom", {"start": v(5315.66, 48.52) * mm, "end": v(5715.66, 48.52) * mm});
            skLineSegment(sketch, "E271.left", {"start": v(5315.66, 498.52) * mm, "end": v(5315.66, 700.71) * mm});
            skLineSegment(sketch, "E271.right", {"start": v(5715.66, 498.52) * mm, "end": v(5715.66, 700.71) * mm});
            skLineSegment(sketch, "E272.bottom", {"start": v(5761.66, 50.71) * mm, "end": v(6161.66, 50.71) * mm});
            skLineSegment(sketch, "E273.bottom", {"start": v(5791.66, 50.71) * mm, "end": v(6191.66, 50.71) * mm});
            skLineSegment(sketch, "E273.left", {"start": v(5791.66, 50.71) * mm, "end": v(5791.66, 700.71) * mm});
            skLineSegment(sketch, "E273.right", {"start": v(6191.66, 50.71) * mm, "end": v(6191.66, 700.71) * mm});
            skLineSegment(sketch, "E274", {"start": v(5953.66, 2686.71) * mm, "end": v(5929.66, 2686.71) * mm});
            skLineSegment(sketch, "E275.trimOffspring", {"start": v(5953.66, 2676.71) * mm, "end": v(6267.66, 2676.71) * mm});
            skLineSegment(sketch, "E276.trimOffspring", {"start": v(6267.66, 2299.71) * mm, "end": v(6267.66, 2249.71) * mm});
            skLineSegment(sketch, "E277.trimOffspring", {"start": v(5929.66, 2299.71) * mm, "end": v(5929.66, 2249.71) * mm});
            skLineSegment(sketch, "E278.trimOffspring", {"start": v(5953.66, 2299.71) * mm, "end": v(5953.66, 2249.71) * mm});
            skLineSegment(sketch, "E279", {"start": v(4423.66, 2686.71) * mm, "end": v(4399.66, 2686.71) * mm});
            skLineSegment(sketch, "E280.trimOffspring", {"start": v(4423.66, 2676.71) * mm, "end": v(4989.66, 2676.71) * mm});
            skLineSegment(sketch, "E281", {"start": v(5013.66, 2686.71) * mm, "end": v(4989.66, 2686.71) * mm});
            skLineSegment(sketch, "E282.trimOffspring", {"start": v(5013.66, 2676.71) * mm, "end": v(5579.66, 2676.71) * mm});
            skLineSegment(sketch, "E283", {"start": v(5603.63, 2686.71) * mm, "end": v(5579.66, 2686.71) * mm});
            skLineSegment(sketch, "E284.trimOffspring", {"start": v(5603.63, 2676.71) * mm, "end": v(5929.66, 2676.71) * mm});
            skLineSegment(sketch, "E285", {"start": v(3328.66, 1857.71) * mm, "end": v(3328.66, 1833.71) * mm});
            skLineSegment(sketch, "E286.trimOffspring", {"start": v(3335.66, 809.71) * mm, "end": v(3335.66, 1554.91) * mm});
            skLineSegment(sketch, "E287.trimOffspring", {"start": v(3328.66, 1572.91) * mm, "end": v(3328.66, 1554.91) * mm});
            skLineSegment(sketch, "E288.trimOffspring", {"start": v(3335.66, 1572.91) * mm, "end": v(3335.66, 1833.71) * mm});
            skLineSegment(sketch, "E289.trimOffspring", {"start": v(3335.66, 1857.71) * mm, "end": v(3335.66, 2231.71) * mm});
            skLineSegment(sketch, "E290.trimOffspring", {"start": v(3335.66, 552.71) * mm, "end": v(3335.66, 785.71) * mm});
            skLineSegment(sketch, "E291", {"start": v(6274.66, 1857.71) * mm, "end": v(6274.66, 1833.71) * mm});
            skLineSegment(sketch, "E292.trimOffspring", {"start": v(6274.66, 1441.21) * mm, "end": v(6274.66, 1423.21) * mm});
            skLineSegment(sketch, "E293.trimOffspring", {"start": v(6267.66, 988.71) * mm, "end": v(6267.66, 809.71) * mm});
            skLineSegment(sketch, "E294.trimOffspring", {"start": v(6267.66, 1833.71) * mm, "end": v(6267.66, 1441.21) * mm});
            skLineSegment(sketch, "E295.trimOffspring", {"start": v(6129.77, 1833.71) * mm, "end": v(6274.66, 1833.71) * mm});
            skLineSegment(sketch, "E296", {"start": v(5946.66, 1857.71) * mm, "end": v(5946.66, 1833.71) * mm});
            skLineSegment(sketch, "E297.trimOffspring", {"start": v(5946.66, 988.71) * mm, "end": v(6274.66, 988.71) * mm});
            skLineSegment(sketch, "E298.trimOffspring", {"start": v(5953.66, 988.71) * mm, "end": v(5953.66, 802.71) * mm});
            skLineSegment(sketch, "E299.trimOffspring", {"start": v(5946.66, 1012.71) * mm, "end": v(6129.77, 1012.71) * mm});
            skLineSegment(sketch, "E300.trimOffspring", {"start": v(5946.66, 1441.21) * mm, "end": v(5946.66, 1423.21) * mm});
            skLineSegment(sketch, "E301.trimOffspring", {"start": v(5946.66, 1857.71) * mm, "end": v(6274.66, 1857.71) * mm});
            skLineSegment(sketch, "E302.trimOffspring", {"start": v(5946.66, 1833.71) * mm, "end": v(6129.77, 1833.71) * mm});
            skLineSegment(sketch, "E303.trimOffspring", {"start": v(5953.66, 1833.71) * mm, "end": v(5953.66, 1441.21) * mm});
            skLineSegment(sketch, "E304", {"start": v(5936.66, 1857.71) * mm, "end": v(5936.66, 1833.71) * mm});
            skLineSegment(sketch, "E305.trimOffspring", {"start": v(5936.66, 1441.21) * mm, "end": v(5936.66, 1423.21) * mm});
            skLineSegment(sketch, "E306.trimOffspring", {"start": v(5929.66, 1833.71) * mm, "end": v(5929.66, 1441.21) * mm});
            skLineSegment(sketch, "E307.trimOffspring", {"start": v(5929.66, 988.71) * mm, "end": v(5929.66, 802.71) * mm});
            skLineSegment(sketch, "E308.trimOffspring", {"start": v(6129.77, 1012.71) * mm, "end": v(6274.66, 1012.71) * mm});
            skLineSegment(sketch, "E309", {"start": v(5013.66, 1850.71) * mm, "end": v(4989.66, 1850.71) * mm});
            skLineSegment(sketch, "E310.trimOffspring", {"start": v(5013.66, 1857.71) * mm, "end": v(5586.66, 1857.71) * mm});
            skLineSegment(sketch, "E311.trimOffspring", {"start": v(5596.63, 1857.71) * mm, "end": v(5596.63, 1833.71) * mm});
            skLineSegment(sketch, "E312.trimOffspring", {"start": v(5596.63, 1441.21) * mm, "end": v(5596.63, 1423.21) * mm});
            skLineSegment(sketch, "E313.trimOffspring", {"start": v(5586.66, 1833.71) * mm, "end": v(5586.66, 1857.71) * mm});
            skLineSegment(sketch, "E314.trimOffspring", {"start": v(5586.66, 988.71) * mm, "end": v(5586.66, 1012.71) * mm});
            skLineSegment(sketch, "E315.trimOffspring", {"start": v(6267.66, 552.71) * mm, "end": v(6267.66, 50.71) * mm});
            skLineSegment(sketch, "E316.trimOffspring", {"start": v(4989.66, 809.71) * mm, "end": v(4423.66, 809.71) * mm});
            skLineSegment(sketch, "E317", {"start": v(5013.66, 995.71) * mm, "end": v(4989.66, 995.71) * mm});
            skLineSegment(sketch, "E318.trimOffspring", {"start": v(5013.66, 988.71) * mm, "end": v(5586.66, 988.71) * mm});
            skLineSegment(sketch, "E319.trimOffspring", {"start": v(3598.97, 1857.71) * mm, "end": v(3598.97, 1833.71) * mm});
            skLineSegment(sketch, "E320.trimOffspring", {"start": v(3598.97, 1857.71) * mm, "end": v(3328.66, 1857.71) * mm});
            skLineSegment(sketch, "E321.trimOffspring", {"start": v(3592.16, 1857.71) * mm, "end": v(3592.16, 2238.71) * mm});
            skLineSegment(sketch, "E322.trimOffspring", {"start": v(3616.16, 1857.71) * mm, "end": v(3616.16, 2238.71) * mm});
            skLineSegment(sketch, "E323.trimOffspring", {"start": v(3598.97, 1833.71) * mm, "end": v(3328.66, 1833.71) * mm});
            skLineSegment(sketch, "E324.trimOffspring", {"start": v(3610.33, 1833.71) * mm, "end": v(3610.33, 1857.71) * mm});
            skLineSegment(sketch, "E325.trimOffspring", {"start": v(3592.16, 1572.91) * mm, "end": v(3328.66, 1572.91) * mm});
            skLineSegment(sketch, "E326.trimOffspring", {"start": v(3335.66, 1554.91) * mm, "end": v(3328.66, 1554.91) * mm});
            skLineSegment(sketch, "E327.trimOffspring", {"start": v(3616.16, 1565.91) * mm, "end": v(3616.16, 1833.71) * mm});
            skLineSegment(sketch, "E328.trimOffspring", {"start": v(4140.3, 2614.89) * mm, "end": v(4140.3, 2299.71) * mm});
            skLineSegment(sketch, "E329.trimOffspring", {"start": v(4116.3, 2615.87) * mm, "end": v(4116.3, 2299.71) * mm});
            skLineSegment(sketch, "E330.trimOffspring", {"start": v(4116.3, 1833.71) * mm, "end": v(4116.3, 1565.91) * mm});
            skLineSegment(sketch, "E331.trimOffspring", {"start": v(4140.3, 1833.71) * mm, "end": v(4140.3, 1565.91) * mm});
            skLineSegment(sketch, "E332.trimOffspring", {"start": v(4123.3, 1833.71) * mm, "end": v(3610.33, 1833.71) * mm});
            skLineSegment(sketch, "E333.trimOffspring", {"start": v(4123.3, 1857.71) * mm, "end": v(3610.33, 1857.71) * mm});
            skLineSegment(sketch, "E334", {"start": v(4416.66, 1857.71) * mm, "end": v(4416.66, 1833.71) * mm});
            skLineSegment(sketch, "E335.trimOffspring", {"start": v(4406.66, 1857.71) * mm, "end": v(4406.66, 1833.71) * mm});
            skLineSegment(sketch, "E336.trimOffspring", {"start": v(4406.66, 1572.91) * mm, "end": v(4406.66, 1554.91) * mm});
            skLineSegment(sketch, "E337.trimOffspring", {"start": v(4399.66, 1554.91) * mm, "end": v(4399.66, 1273.31) * mm});
            skLineSegment(sketch, "E338.trimOffspring", {"start": v(4399.66, 1273.31) * mm, "end": v(4399.66, 988.71) * mm});
            skLineSegment(sketch, "E339", {"start": v(4416.66, 1012.71) * mm, "end": v(4416.66, 988.71) * mm});
            skLineSegment(sketch, "E340.trimOffspring", {"start": v(3592.16, 1565.91) * mm, "end": v(3592.16, 1833.71) * mm});
            skLineSegment(sketch, "E341", {"start": v(3616.16, 1572.91) * mm, "end": v(4116.3, 1572.91) * mm});
            skLineSegment(sketch, "E342.0", {"start": v(3887.66, 700.71) * mm, "end": v(4287.66, 700.71) * mm});
            skLineSegment(sketch, "E343.0", {"start": v(3411.66, 700.71) * mm, "end": v(3811.66, 700.71) * mm});
            skLineSegment(sketch, "E344", {"start": v(3811.66, 700.71) * mm, "end": v(3811.66, 500.71) * mm});
            skLineSegment(sketch, "E345", {"start": v(3411.66, 700.71) * mm, "end": v(3411.66, 500.71) * mm});
            skLineSegment(sketch, "E346", {"start": v(3887.66, 700.71) * mm, "end": v(3887.66, 500.71) * mm});
            skLineSegment(sketch, "E347", {"start": v(4287.66, 700.71) * mm, "end": v(4287.66, 500.71) * mm});
            skLineSegment(sketch, "E348", {"start": v(5596.63, 1423.21) * mm, "end": v(5936.66, 1423.21) * mm});
            skLineSegment(sketch, "E349.0", {"start": v(5596.63, 1441.21) * mm, "end": v(5936.66, 1441.21) * mm});
            skPoint(sketch, "E350.orphan", {"position": v(5603.66, 1423.21) * mm});
            skLineSegment(sketch, "E351.trimOffspring", {"start": v(5603.66, 1423.21) * mm, "end": v(5603.66, 1012.71) * mm});
            skLineSegment(sketch, "E352.trimOffspring", {"start": v(5596.63, 1012.71) * mm, "end": v(5596.63, 988.71) * mm});
            skPoint(sketch, "E353.orphan", {"position": v(6267.66, 1423.21) * mm});
            skLineSegment(sketch, "E354.trimOffspring", {"start": v(6267.66, 1423.21) * mm, "end": v(6267.66, 1012.71) * mm});
            skLineSegment(sketch, "E355.trimOffspring", {"start": v(6274.66, 1012.71) * mm, "end": v(6274.66, 988.71) * mm});
            skLineSegment(sketch, "E356", {"start": v(5936.66, 1012.71) * mm, "end": v(5936.66, 988.71) * mm});
            skLineSegment(sketch, "E357", {"start": v(5946.66, 1012.71) * mm, "end": v(5946.66, 988.71) * mm});
            skLineSegment(sketch, "E358.trimOffspring", {"start": v(5953.66, 1423.21) * mm, "end": v(5953.66, 1012.71) * mm});
            skLineSegment(sketch, "E359.trimOffspring", {"start": v(5929.66, 1423.21) * mm, "end": v(5929.66, 1012.71) * mm});
            skLineSegment(sketch, "E360.trimOffspring", {"start": v(5946.66, 1423.21) * mm, "end": v(6274.66, 1423.21) * mm});
            skLineSegment(sketch, "E361.trimOffspring", {"start": v(5946.66, 1441.21) * mm, "end": v(6274.66, 1441.21) * mm});
            skLineSegment(sketch, "E362.trimOffspring", {"start": v(4116.3, 2299.71) * mm, "end": v(4116.3, 2249.71) * mm});
            skLineSegment(sketch, "E363.trimOffspring", {"start": v(4140.3, 2299.71) * mm, "end": v(4140.3, 2249.71) * mm});
            skLineSegment(sketch, "E364.trimOffspring", {"start": v(4140.3, 2614.89) * mm, "end": v(4291.38, 2676.71) * mm});
            skLineSegment(sketch, "E365.trimOffspring", {"start": v(4116.3, 2615.87) * mm, "end": v(4136.5, 2624.14) * mm});
            skLineSegment(sketch, "E366", {"start": v(4399.66, 2686.71) * mm, "end": v(4399.66, 2299.71) * mm});
            skLineSegment(sketch, "E367", {"start": v(4423.66, 2686.71) * mm, "end": v(4423.66, 2299.71) * mm});
            skLineSegment(sketch, "E368", {"start": v(4989.66, 2299.71) * mm, "end": v(4989.66, 2686.71) * mm});
            skLineSegment(sketch, "E369", {"start": v(5013.66, 2686.71) * mm, "end": v(5013.66, 2299.71) * mm});
            skLineSegment(sketch, "E370", {"start": v(5579.66, 2686.71) * mm, "end": v(5579.66, 2299.71) * mm});
            skLineSegment(sketch, "E371", {"start": v(5603.63, 2299.71) * mm, "end": v(5603.63, 2686.71) * mm});
            skLineSegment(sketch, "E372", {"start": v(5929.66, 2686.71) * mm, "end": v(5929.66, 2299.71) * mm});
            skLineSegment(sketch, "E373", {"start": v(5953.66, 2676.71) * mm, "end": v(5953.66, 2299.71) * mm});
            skLineSegment(sketch, "E374", {"start": v(6267.66, 2676.71) * mm, "end": v(6267.66, 2299.71) * mm});
            skLineSegment(sketch, "E375.trimOffspring", {"start": v(4399.66, 809.71) * mm, "end": v(3328.66, 809.71) * mm});
            skLineSegment(sketch, "E376.0", {"start": v(3592.16, 1565.91) * mm, "end": v(3616.16, 1565.91) * mm});
            skLineSegment(sketch, "E377.trimOffspring", {"start": v(4116.3, 1565.91) * mm, "end": v(4140.3, 1565.91) * mm});
            skLineSegment(sketch, "E378", {"start": v(4399.66, 1554.91) * mm, "end": v(3335.66, 1554.91) * mm});
            skLineSegment(sketch, "E379.trimOffspring", {"start": v(6267.66, 576.71) * mm, "end": v(6267.66, 552.71) * mm});
            skLineSegment(sketch, "E380.trimOffspring", {"start": v(3335.66, 2285.6) * mm, "end": v(4116.3, 2605.06) * mm});
            skLineSegment(sketch, "E381", {"start": v(5315.66, 498.52) * mm, "end": v(5315.66, 48.52) * mm});
            skLineSegment(sketch, "E382", {"start": v(5715.66, 498.52) * mm, "end": v(5715.66, 48.52) * mm});
            skLineSegment(sketch, "E383.trimOffspring", {"start": v(4363.66, 700.71) * mm, "end": v(4763.66, 700.71) * mm});
            skLineSegment(sketch, "E384.trimOffspring", {"start": v(4839.66, 700.71) * mm, "end": v(5239.66, 700.71) * mm});
            skLineSegment(sketch, "E385.trimOffspring", {"start": v(5315.66, 700.71) * mm, "end": v(5715.66, 700.71) * mm});
            skLineSegment(sketch, "E386.trimOffspring", {"start": v(5791.66, 700.71) * mm, "end": v(6191.66, 700.71) * mm});
            skLineSegment(sketch, "E387", {"start": v(6267.66, 600.71) * mm, "end": v(6267.66, 576.71) * mm});
            skLineSegment(sketch, "E388.0", {"start": v(5953.66, 802.71) * mm, "end": v(5929.66, 802.71) * mm});
            skLineSegment(sketch, "E389.trimOffspring", {"start": v(5929.66, 809.71) * mm, "end": v(5603.66, 809.71) * mm});
            skLineSegment(sketch, "E390.trimOffspring", {"start": v(5579.66, 809.71) * mm, "end": v(5013.66, 809.71) * mm});
            skLineSegment(sketch, "E391.trimOffspring", {"start": v(5603.66, 802.71) * mm, "end": v(5579.66, 802.71) * mm});
            skLineSegment(sketch, "E392.trimOffspring", {"start": v(4423.66, 802.71) * mm, "end": v(4399.66, 802.71) * mm});
            skLineSegment(sketch, "E393.trimOffspring", {"start": v(5013.66, 802.71) * mm, "end": v(4989.66, 802.71) * mm});
            skLineSegment(sketch, "E394.trimOffspring", {"start": v(6274.66, 809.71) * mm, "end": v(6274.66, 785.71) * mm});
            skLineSegment(sketch, "E395.trimOffspring", {"start": v(6267.66, 785.71) * mm, "end": v(6267.66, 600.71) * mm});
            skLineSegment(sketch, "E396", {"start": v(4286.66, 2700.71) * mm, "end": v(4291.38, 2676.71) * mm});
            skLineSegment(sketch, "E397", {"start": v(3328.66, 2249.71) * mm, "end": v(3328.66, 2231.71) * mm});
            skLineSegment(sketch, "E398", {"start": v(3328.66, 2231.71) * mm, "end": v(3335.66, 2231.71) * mm});
            skLineSegment(sketch, "E399.0", {"start": v(3328.66, 2231.71) * mm, "end": v(3592.16, 2231.71) * mm});
            skLineSegment(sketch, "E400.0", {"start": v(3328.66, 2249.71) * mm, "end": v(3610.33, 2249.71) * mm});
            skLineSegment(sketch, "E401", {"start": v(6274.66, 2249.71) * mm, "end": v(6274.66, 2231.71) * mm});
            skLineSegment(sketch, "E402", {"start": v(5946.66, 2249.71) * mm, "end": v(5946.66, 2231.71) * mm});
            skLineSegment(sketch, "E403", {"start": v(5936.66, 2249.71) * mm, "end": v(5936.66, 2231.71) * mm});
            skLineSegment(sketch, "E404.trimOffspring", {"start": v(5946.66, 2249.71) * mm, "end": v(6274.66, 2249.71) * mm});
            skLineSegment(sketch, "E405.trimOffspring", {"start": v(5946.66, 2231.71) * mm, "end": v(6274.66, 2231.71) * mm});
            skLineSegment(sketch, "E406.trimOffspring", {"start": v(5596.63, 2249.71) * mm, "end": v(5596.63, 2231.71) * mm});
            skLineSegment(sketch, "E407.trimOffspring", {"start": v(5596.63, 2249.71) * mm, "end": v(5936.66, 2249.71) * mm});
            skLineSegment(sketch, "E408.trimOffspring", {"start": v(5596.63, 2231.71) * mm, "end": v(5936.66, 2231.71) * mm});
            skLineSegment(sketch, "E409.trimOffspring", {"start": v(5586.66, 2231.71) * mm, "end": v(5586.66, 2249.71) * mm});
            skLineSegment(sketch, "E410", {"start": v(5006.66, 2249.71) * mm, "end": v(5006.66, 2231.71) * mm});
            skLineSegment(sketch, "E411", {"start": v(4996.66, 2249.71) * mm, "end": v(4996.66, 2231.71) * mm});
            skLineSegment(sketch, "E412.trimOffspring", {"start": v(5006.66, 2249.71) * mm, "end": v(5586.66, 2249.71) * mm});
            skLineSegment(sketch, "E413.trimOffspring", {"start": v(5006.66, 2231.71) * mm, "end": v(5586.66, 2231.71) * mm});
            skLineSegment(sketch, "E414.trimOffspring", {"start": v(3610.33, 2249.71) * mm, "end": v(4123.3, 2249.71) * mm});
            skLineSegment(sketch, "E415.trimOffspring", {"start": v(3616.16, 2231.71) * mm, "end": v(4123.3, 2231.71) * mm});
            skLineSegment(sketch, "E416.trimOffspring", {"start": v(4133.3, 2249.71) * mm, "end": v(4406.66, 2249.71) * mm});
            skLineSegment(sketch, "E417.trimOffspring", {"start": v(4133.3, 2231.71) * mm, "end": v(4406.66, 2231.71) * mm});
            skLineSegment(sketch, "E418.trimOffspring", {"start": v(4123.3, 2249.71) * mm, "end": v(4123.3, 2231.71) * mm});
            skLineSegment(sketch, "E419", {"start": v(4416.66, 2249.71) * mm, "end": v(4416.66, 2231.71) * mm});
            skLineSegment(sketch, "E420.trimOffspring", {"start": v(4416.66, 2249.71) * mm, "end": v(4996.66, 2249.71) * mm});
            skLineSegment(sketch, "E421.trimOffspring", {"start": v(4416.66, 2231.71) * mm, "end": v(4996.66, 2231.71) * mm});
            skLineSegment(sketch, "E422.trimOffspring", {"start": v(4406.66, 2249.71) * mm, "end": v(4406.66, 2231.71) * mm});
            skLineSegment(sketch, "E423.trimOffspring", {"start": v(4116.3, 2231.71) * mm, "end": v(4116.3, 1857.71) * mm});
            skLineSegment(sketch, "E424.trimOffspring", {"start": v(4140.3, 2231.71) * mm, "end": v(4140.3, 1857.71) * mm});
            skLineSegment(sketch, "E425.trimOffspring", {"start": v(4399.66, 2249.71) * mm, "end": v(4399.66, 2299.71) * mm});
            skLineSegment(sketch, "E426.trimOffspring", {"start": v(4423.66, 2249.71) * mm, "end": v(4423.66, 2299.71) * mm});
            skLineSegment(sketch, "E427.trimOffspring", {"start": v(4989.66, 2249.71) * mm, "end": v(4989.66, 2299.71) * mm});
            skLineSegment(sketch, "E428.trimOffspring", {"start": v(5013.66, 2249.71) * mm, "end": v(5013.66, 2299.71) * mm});
            skLineSegment(sketch, "E429.trimOffspring", {"start": v(5579.66, 2249.71) * mm, "end": v(5579.66, 2299.71) * mm});
            skLineSegment(sketch, "E430.trimOffspring", {"start": v(5603.63, 2249.71) * mm, "end": v(5603.63, 2299.71) * mm});
            skLineSegment(sketch, "E431.trimOffspring", {"start": v(5929.66, 2231.71) * mm, "end": v(5929.66, 1857.71) * mm});
            skLineSegment(sketch, "E432.trimOffspring", {"start": v(5953.66, 2231.71) * mm, "end": v(5953.66, 1857.71) * mm});
            skLineSegment(sketch, "E433.trimOffspring", {"start": v(6267.66, 2231.71) * mm, "end": v(6267.66, 1857.71) * mm});
            skLineSegment(sketch, "E434", {"start": v(3311.66, 2301.71) * mm, "end": v(3335.66, 2285.6) * mm});
            skLineSegment(sketch, "E435.trimOffspring", {"start": v(3335.66, 2249.71) * mm, "end": v(3335.66, 2285.6) * mm});
            skLineSegment(sketch, "E436", {"start": v(4123.3, 1857.71) * mm, "end": v(4123.3, 1833.71) * mm});
            skLineSegment(sketch, "E437.0", {"start": v(6274.66, 785.71) * mm, "end": v(3328.66, 785.71) * mm});
            skLineSegment(sketch, "E438", {"start": v(3328.66, 809.71) * mm, "end": v(3328.66, 785.71) * mm});
            skLineSegment(sketch, "E439.0", {"start": v(4286.66, 2688.71) * mm, "end": v(4289.02, 2688.71) * mm});
            skLineSegment(sketch, "E440", {"start": v(4140.3, 2614.89) * mm, "end": v(4136.5, 2624.14) * mm});
            skLineSegment(sketch, "E441", {"start": v(6267.66, 2676.71) * mm, "end": v(6291.66, 2700.71) * mm});
            skLineSegment(sketch, "E442.0", {"start": v(4133.3, 2231.71) * mm, "end": v(4133.3, 2249.71) * mm});
            skLineSegment(sketch, "E443.0", {"start": v(4133.3, 1833.71) * mm, "end": v(4133.3, 1857.71) * mm});
            skLineSegment(sketch, "E444.0", {"start": v(3592.16, 2238.71) * mm, "end": v(3616.16, 2238.71) * mm});
            skSolve(sketch);
        }
        {
            var Q0;
            Q0=qCreatedBy(makeId("Front.planeOp"),FACE);
            var sketch = newSketch(context, id + "F3", { "sketchPlane" : qUnion([Q0])});
            skLineSegment(sketch, "E445", {"start": v(-1676.04, 0) * mm, "end": v(-1676.04, 2251) * mm});
            skLineSegment(sketch, "E446", {"start": v(-1676.04, 2251) * mm, "end": v(-701.04, 2650) * mm});
            skLineSegment(sketch, "E447", {"start": v(-701.04, 2650) * mm, "end": v(2257.32, 2650) * mm});
            skLineSegment(sketch, "E448", {"start": v(2257.32, 2650) * mm, "end": v(3223.96, 2240) * mm});
            skLineSegment(sketch, "E449", {"start": v(3223.96, 2240) * mm, "end": v(3223.96, 0) * mm});
            skLineSegment(sketch, "E450", {"start": v(3223.96, 0) * mm, "end": v(-1676.04, 0) * mm});
            skLineSegment(sketch, "E451", {"start": v(2873.96, 0) * mm, "end": v(2873.96, 2100) * mm});
            skLineSegment(sketch, "E452", {"start": v(2873.96, 2100) * mm, "end": v(1673.96, 2100) * mm});
            skLineSegment(sketch, "E453", {"start": v(1673.96, 2100) * mm, "end": v(1673.96, 0) * mm});
            skLineSegment(sketch, "E454.bottom", {"start": v(-476.04, 1695) * mm, "end": v(503.96, 1695) * mm});
            skLineSegment(sketch, "E454.top", {"start": v(-476.04, 1050) * mm, "end": v(503.96, 1050) * mm});
            skLineSegment(sketch, "E454.left", {"start": v(-476.04, 1695) * mm, "end": v(-476.04, 1050) * mm});
            skLineSegment(sketch, "E454.right", {"start": v(503.96, 1695) * mm, "end": v(503.96, 1050) * mm});
            skLineSegment(sketch, "E455", {"start": v(1303.96, 2650) * mm, "end": v(1303.96, 0) * mm});
            skLineSegment(sketch, "E456.0", {"start": v(-1652.04, 0) * mm, "end": v(-1652.04, 502) * mm});
            skLineSegment(sketch, "E457.0", {"start": v(-696.32, 2626) * mm, "end": v(-588.04, 2626) * mm});
            skLineSegment(sketch, "E458.0", {"start": v(965.96, 2636) * mm, "end": v(965.96, 2626) * mm});
            skLineSegment(sketch, "E459.0", {"start": v(615.93, 1807) * mm, "end": v(615.93, 2181) * mm});
            skLineSegment(sketch, "E460.0", {"start": v(591.96, 1807) * mm, "end": v(591.96, 2181) * mm});
            skLineSegment(sketch, "E461.0", {"start": v(591.96, 1783) * mm, "end": v(591.96, 962) * mm});
            skLineSegment(sketch, "E462.0", {"start": v(615.96, 1783) * mm, "end": v(615.96, 1390.5) * mm});
            skLineSegment(sketch, "E463.0", {"start": v(615.96, 938) * mm, "end": v(615.96, 752) * mm});
            skLineSegment(sketch, "E464.0", {"start": v(591.96, 938) * mm, "end": v(591.96, 752) * mm});
            skLineSegment(sketch, "E465.0", {"start": v(25.96, 1800) * mm, "end": v(25.96, 2181) * mm});
            skLineSegment(sketch, "E466.0", {"start": v(1.96, 1800) * mm, "end": v(1.96, 2181) * mm});
            skLineSegment(sketch, "E467.0", {"start": v(-564.04, 1807) * mm, "end": v(-564.04, 2181) * mm});
            skLineSegment(sketch, "E468.0", {"start": v(-588.04, 1807) * mm, "end": v(-588.04, 2181) * mm});
            skLineSegment(sketch, "E469.0", {"start": v(-588.04, 1783) * mm, "end": v(-588.04, 1522.2) * mm});
            skLineSegment(sketch, "E470.0", {"start": v(-564.04, 1783) * mm, "end": v(-564.04, 1222.6) * mm});
            skLineSegment(sketch, "E471.0", {"start": v(-588.04, 938) * mm, "end": v(-588.04, 752) * mm});
            skLineSegment(sketch, "E472.0", {"start": v(-564.04, 938) * mm, "end": v(-564.04, 752) * mm});
            skLineSegment(sketch, "E473.0", {"start": v(-571.04, 1783) * mm, "end": v(598.96, 1783) * mm});
            skLineSegment(sketch, "E474.0", {"start": v(-571.04, 1807) * mm, "end": v(1.96, 1807) * mm});
            skLineSegment(sketch, "E475.0", {"start": v(-571.04, 938) * mm, "end": v(1.96, 938) * mm});
            skLineSegment(sketch, "E476.0", {"start": v(-571.04, 962) * mm, "end": v(598.96, 962) * mm});
            skLineSegment(sketch, "E477.0", {"start": v(-581.04, 1807) * mm, "end": v(-854, 1807) * mm});
            skLineSegment(sketch, "E478.0", {"start": v(-581.04, 1783) * mm, "end": v(-854, 1783) * mm});
            skLineSegment(sketch, "E479.0", {"start": v(608.93, 938) * mm, "end": v(948.96, 938) * mm});
            skLineSegment(sketch, "E480.0", {"start": v(608.93, 962) * mm, "end": v(948.96, 962) * mm});
            skLineSegment(sketch, "E481.0", {"start": v(608.93, 1783) * mm, "end": v(948.96, 1783) * mm});
            skLineSegment(sketch, "E482.0", {"start": v(608.93, 1807) * mm, "end": v(948.96, 1807) * mm});
            skLineSegment(sketch, "E483.0", {"start": v(1.96, 945) * mm, "end": v(1.96, 752) * mm});
            skLineSegment(sketch, "E484.0", {"start": v(25.96, 945) * mm, "end": v(25.96, 752) * mm});
            skLineSegment(sketch, "E485.0", {"start": v(-581.04, 1522.2) * mm, "end": v(-847.4, 1522.2) * mm});
            skLineSegment(sketch, "E486.0", {"start": v(-581.04, 1504.2) * mm, "end": v(-588.04, 1504.2) * mm});
            skLineSegment(sketch, "E487.0", {"start": v(1286.96, 759) * mm, "end": v(965.96, 759) * mm});
            skLineSegment(sketch, "E488.0", {"start": v(1286.96, 741) * mm, "end": v(18.96, 741) * mm});
            skLineSegment(sketch, "E489", {"start": v(-564.04, 1222.6) * mm, "end": v(-564.04, 962) * mm});
            skLineSegment(sketch, "E490.bottom", {"start": v(-1576.04, 0) * mm, "end": v(-1176.04, 0) * mm});
            skLineSegment(sketch, "E490.left", {"start": v(-1576.04, 0) * mm, "end": v(-1576.04, 450) * mm});
            skLineSegment(sketch, "E490.right", {"start": v(-1176.04, 0) * mm, "end": v(-1176.04, 450) * mm});
            skLineSegment(sketch, "E491.bottom", {"start": v(-1100.04, 0) * mm, "end": v(-700.04, 0) * mm});
            skLineSegment(sketch, "E491.left", {"start": v(-1100.04, 0) * mm, "end": v(-1100.04, 450) * mm});
            skLineSegment(sketch, "E491.right", {"start": v(-700.04, 0) * mm, "end": v(-700.04, 450) * mm});
            skLineSegment(sketch, "E492.bottom", {"start": v(-624.04, 0) * mm, "end": v(-224.04, 0) * mm});
            skLineSegment(sketch, "E492.left", {"start": v(-624.04, 0) * mm, "end": v(-624.04, 650) * mm});
            skLineSegment(sketch, "E492.right", {"start": v(-224.04, 0) * mm, "end": v(-224.04, 650) * mm});
            skLineSegment(sketch, "E493.bottom", {"start": v(-148.04, 0) * mm, "end": v(251.96, 0) * mm});
            skLineSegment(sketch, "E493.left", {"start": v(-148.04, 0) * mm, "end": v(-148.04, 650) * mm});
            skLineSegment(sketch, "E493.right", {"start": v(251.96, 0) * mm, "end": v(251.96, 650) * mm});
            skLineSegment(sketch, "E494.bottom", {"start": v(327.96, -2.2) * mm, "end": v(727.96, -2.2) * mm});
            skLineSegment(sketch, "E494.left", {"start": v(327.96, 447.8) * mm, "end": v(327.96, 650) * mm});
            skLineSegment(sketch, "E494.right", {"start": v(727.96, 447.8) * mm, "end": v(727.96, 650) * mm});
            skLineSegment(sketch, "E495.bottom", {"start": v(773.96, 0) * mm, "end": v(1173.96, 0) * mm});
            skLineSegment(sketch, "E496.bottom", {"start": v(803.96, 0) * mm, "end": v(1203.96, 0) * mm});
            skLineSegment(sketch, "E496.left", {"start": v(803.96, 0) * mm, "end": v(803.96, 650) * mm});
            skLineSegment(sketch, "E496.right", {"start": v(1203.96, 0) * mm, "end": v(1203.96, 650) * mm});
            skLineSegment(sketch, "E497", {"start": v(965.96, 2636) * mm, "end": v(941.96, 2636) * mm});
            skLineSegment(sketch, "E498.trimOffspring", {"start": v(965.96, 2626) * mm, "end": v(1279.96, 2626) * mm});
            skLineSegment(sketch, "E499", {"start": v(1279.96, 2626) * mm, "end": v(1303.96, 2650) * mm});
            skLineSegment(sketch, "E500.trimOffspring", {"start": v(1279.96, 2249) * mm, "end": v(1279.96, 2199) * mm});
            skLineSegment(sketch, "E501.trimOffspring", {"start": v(941.96, 2249) * mm, "end": v(941.96, 2199) * mm});
            skLineSegment(sketch, "E502.trimOffspring", {"start": v(965.96, 2249) * mm, "end": v(965.96, 2199) * mm});
            skLineSegment(sketch, "E503", {"start": v(-564.04, 2636) * mm, "end": v(-588.04, 2636) * mm});
            skLineSegment(sketch, "E504.trimOffspring", {"start": v(-564.04, 2626) * mm, "end": v(1.96, 2626) * mm});
            skLineSegment(sketch, "E505", {"start": v(25.96, 2636) * mm, "end": v(1.96, 2636) * mm});
            skLineSegment(sketch, "E506.trimOffspring", {"start": v(25.96, 2626) * mm, "end": v(591.96, 2626) * mm});
            skLineSegment(sketch, "E507", {"start": v(615.93, 2636) * mm, "end": v(591.96, 2636) * mm});
            skLineSegment(sketch, "E508.trimOffspring", {"start": v(615.93, 2626) * mm, "end": v(941.96, 2626) * mm});
            skLineSegment(sketch, "E509", {"start": v(-1659.04, 1807) * mm, "end": v(-1659.04, 1783) * mm});
            skLineSegment(sketch, "E510.trimOffspring", {"start": v(-1659.04, 759) * mm, "end": v(-1659.04, 741) * mm});
            skLineSegment(sketch, "E511.trimOffspring", {"start": v(-1652.04, 759) * mm, "end": v(-1652.04, 1504.2) * mm});
            skLineSegment(sketch, "E512.trimOffspring", {"start": v(-1659.04, 1522.2) * mm, "end": v(-1659.04, 1504.2) * mm});
            skLineSegment(sketch, "E513.trimOffspring", {"start": v(-1652.04, 1522.2) * mm, "end": v(-1652.04, 1783) * mm});
            skLineSegment(sketch, "E514.trimOffspring", {"start": v(-1652.04, 1807) * mm, "end": v(-1652.04, 2181) * mm});
            skLineSegment(sketch, "E515.trimOffspring", {"start": v(-1652.04, 502) * mm, "end": v(-1652.04, 741) * mm});
            skLineSegment(sketch, "E516", {"start": v(1286.96, 1807) * mm, "end": v(1286.96, 1783) * mm});
            skLineSegment(sketch, "E517.trimOffspring", {"start": v(1286.96, 1390.5) * mm, "end": v(1286.96, 1372.5) * mm});
            skLineSegment(sketch, "E518.trimOffspring", {"start": v(1279.96, 938) * mm, "end": v(1279.96, 759) * mm});
            skLineSegment(sketch, "E519.trimOffspring", {"start": v(1279.96, 1783) * mm, "end": v(1279.96, 1390.5) * mm});
            skLineSegment(sketch, "E520.trimOffspring", {"start": v(1142.08, 1783) * mm, "end": v(1286.96, 1783) * mm});
            skLineSegment(sketch, "E521", {"start": v(958.96, 1807) * mm, "end": v(958.96, 1783) * mm});
            skLineSegment(sketch, "E522.trimOffspring", {"start": v(958.96, 938) * mm, "end": v(1286.96, 938) * mm});
            skLineSegment(sketch, "E523.trimOffspring", {"start": v(965.96, 938) * mm, "end": v(965.96, 752) * mm});
            skLineSegment(sketch, "E524.trimOffspring", {"start": v(958.96, 962) * mm, "end": v(1142.08, 962) * mm});
            skLineSegment(sketch, "E525.trimOffspring", {"start": v(958.96, 1390.5) * mm, "end": v(958.96, 1372.5) * mm});
            skLineSegment(sketch, "E526.trimOffspring", {"start": v(958.96, 1807) * mm, "end": v(1286.96, 1807) * mm});
            skLineSegment(sketch, "E527.trimOffspring", {"start": v(958.96, 1783) * mm, "end": v(1142.08, 1783) * mm});
            skLineSegment(sketch, "E528.trimOffspring", {"start": v(965.96, 1783) * mm, "end": v(965.96, 1390.5) * mm});
            skLineSegment(sketch, "E529", {"start": v(948.96, 1807) * mm, "end": v(948.96, 1783) * mm});
            skLineSegment(sketch, "E530.trimOffspring", {"start": v(948.96, 1390.5) * mm, "end": v(948.96, 1372.5) * mm});
            skLineSegment(sketch, "E531.trimOffspring", {"start": v(941.96, 1783) * mm, "end": v(941.96, 1390.5) * mm});
            skLineSegment(sketch, "E532.trimOffspring", {"start": v(941.96, 938) * mm, "end": v(941.96, 752) * mm});
            skLineSegment(sketch, "E533.trimOffspring", {"start": v(1142.08, 962) * mm, "end": v(1286.96, 962) * mm});
            skLineSegment(sketch, "E534", {"start": v(25.96, 1800) * mm, "end": v(1.96, 1800) * mm});
            skLineSegment(sketch, "E535.trimOffspring", {"start": v(25.96, 1807) * mm, "end": v(598.96, 1807) * mm});
            skLineSegment(sketch, "E536.trimOffspring", {"start": v(608.93, 1807) * mm, "end": v(608.93, 1783) * mm});
            skLineSegment(sketch, "E537.trimOffspring", {"start": v(608.93, 1390.5) * mm, "end": v(608.93, 1372.5) * mm});
            skLineSegment(sketch, "E538.trimOffspring", {"start": v(598.96, 1783) * mm, "end": v(598.96, 1807) * mm});
            skLineSegment(sketch, "E539.trimOffspring", {"start": v(598.96, 938) * mm, "end": v(598.96, 962) * mm});
            skLineSegment(sketch, "E540.trimOffspring", {"start": v(1279.96, 502) * mm, "end": v(1279.96, 0) * mm});
            skLineSegment(sketch, "E541.trimOffspring", {"start": v(1.96, 759) * mm, "end": v(-564.04, 759) * mm});
            skLineSegment(sketch, "E542.trimOffspring", {"start": v(8.96, 741) * mm, "end": v(-571.04, 741) * mm});
            skLineSegment(sketch, "E543", {"start": v(25.96, 945) * mm, "end": v(1.96, 945) * mm});
            skLineSegment(sketch, "E544.trimOffspring", {"start": v(25.96, 938) * mm, "end": v(598.96, 938) * mm});
            skLineSegment(sketch, "E545.trimOffspring", {"start": v(-1388.73, 1807) * mm, "end": v(-1388.73, 1783) * mm});
            skLineSegment(sketch, "E546.trimOffspring", {"start": v(-1388.73, 1807) * mm, "end": v(-1659.04, 1807) * mm});
            skLineSegment(sketch, "E547.trimOffspring", {"start": v(-1395.53, 1807) * mm, "end": v(-1395.53, 2186) * mm});
            skLineSegment(sketch, "E548.trimOffspring", {"start": v(-1371.53, 1807) * mm, "end": v(-1371.53, 2186) * mm});
            skLineSegment(sketch, "E549.trimOffspring", {"start": v(-1388.73, 1783) * mm, "end": v(-1659.04, 1783) * mm});
            skLineSegment(sketch, "E550.trimOffspring", {"start": v(-1377.37, 1783) * mm, "end": v(-1377.37, 1807) * mm});
            skLineSegment(sketch, "E551.trimOffspring", {"start": v(-1395.53, 1522.2) * mm, "end": v(-1659.04, 1522.2) * mm});
            skLineSegment(sketch, "E552.trimOffspring", {"start": v(-1652.04, 1504.2) * mm, "end": v(-1659.04, 1504.2) * mm});
            skLineSegment(sketch, "E553.trimOffspring", {"start": v(-1371.53, 1515.2) * mm, "end": v(-1371.53, 1783) * mm});
            skLineSegment(sketch, "E554.trimOffspring", {"start": v(-847.4, 2564.17) * mm, "end": v(-847.4, 2249) * mm});
            skLineSegment(sketch, "E555.trimOffspring", {"start": v(-871.4, 2565.16) * mm, "end": v(-871.4, 2249) * mm});
            skLineSegment(sketch, "E556.trimOffspring", {"start": v(-871.4, 1783) * mm, "end": v(-871.4, 1515.2) * mm});
            skLineSegment(sketch, "E557.trimOffspring", {"start": v(-847.4, 1783) * mm, "end": v(-847.4, 1515.2) * mm});
            skLineSegment(sketch, "E558.trimOffspring", {"start": v(-864.4, 1783) * mm, "end": v(-1377.37, 1783) * mm});
            skLineSegment(sketch, "E559.trimOffspring", {"start": v(-864.4, 1807) * mm, "end": v(-1377.37, 1807) * mm});
            skLineSegment(sketch, "E560.trimOffspring", {"start": v(-854, 1783) * mm, "end": v(-854, 1807) * mm});
            skLineSegment(sketch, "E561", {"start": v(-571.04, 1807) * mm, "end": v(-571.04, 1783) * mm});
            skLineSegment(sketch, "E562.trimOffspring", {"start": v(-581.04, 1807) * mm, "end": v(-581.04, 1783) * mm});
            skLineSegment(sketch, "E563.trimOffspring", {"start": v(-581.04, 1522.2) * mm, "end": v(-581.04, 1504.2) * mm});
            skLineSegment(sketch, "E564.trimOffspring", {"start": v(-588.04, 1504.2) * mm, "end": v(-588.04, 1222.6) * mm});
            skLineSegment(sketch, "E565.trimOffspring", {"start": v(-588.04, 1222.6) * mm, "end": v(-588.04, 938) * mm});
            skLineSegment(sketch, "E566", {"start": v(-571.04, 962) * mm, "end": v(-571.04, 938) * mm});
            skLineSegment(sketch, "E567.trimOffspring", {"start": v(-1395.53, 1515.2) * mm, "end": v(-1395.53, 1783) * mm});
            skLineSegment(sketch, "E568", {"start": v(-564.04, 741) * mm, "end": v(-571.04, 741) * mm});
            skLineSegment(sketch, "E569", {"start": v(-1371.53, 1522.2) * mm, "end": v(-871.4, 1522.2) * mm});
            skLineSegment(sketch, "E570.0", {"start": v(-1100.04, 650) * mm, "end": v(-700.04, 650) * mm});
            skLineSegment(sketch, "E571.0", {"start": v(-1576.04, 650) * mm, "end": v(-1176.04, 650) * mm});
            skLineSegment(sketch, "E572", {"start": v(-1176.04, 650) * mm, "end": v(-1176.04, 450) * mm});
            skLineSegment(sketch, "E573", {"start": v(-1576.04, 650) * mm, "end": v(-1576.04, 450) * mm});
            skLineSegment(sketch, "E574", {"start": v(-1100.04, 650) * mm, "end": v(-1100.04, 450) * mm});
            skLineSegment(sketch, "E575", {"start": v(-700.04, 650) * mm, "end": v(-700.04, 450) * mm});
            skLineSegment(sketch, "E576", {"start": v(608.93, 1372.5) * mm, "end": v(948.96, 1372.5) * mm});
            skLineSegment(sketch, "E577.0", {"start": v(608.93, 1390.5) * mm, "end": v(948.96, 1390.5) * mm});
            skPoint(sketch, "E578.orphan", {"position": v(615.96, 1372.5) * mm});
            skLineSegment(sketch, "E579.trimOffspring", {"start": v(615.96, 1372.5) * mm, "end": v(615.96, 962) * mm});
            skLineSegment(sketch, "E580.trimOffspring", {"start": v(608.93, 962) * mm, "end": v(608.93, 938) * mm});
            skPoint(sketch, "E581.orphan", {"position": v(1279.96, 1372.5) * mm});
            skLineSegment(sketch, "E582.trimOffspring", {"start": v(1279.96, 1372.5) * mm, "end": v(1279.96, 962) * mm});
            skLineSegment(sketch, "E583.trimOffspring", {"start": v(1286.96, 962) * mm, "end": v(1286.96, 938) * mm});
            skLineSegment(sketch, "E584", {"start": v(948.96, 962) * mm, "end": v(948.96, 938) * mm});
            skLineSegment(sketch, "E585", {"start": v(958.96, 962) * mm, "end": v(958.96, 938) * mm});
            skLineSegment(sketch, "E586.trimOffspring", {"start": v(965.96, 1372.5) * mm, "end": v(965.96, 962) * mm});
            skLineSegment(sketch, "E587.trimOffspring", {"start": v(941.96, 1372.5) * mm, "end": v(941.96, 962) * mm});
            skLineSegment(sketch, "E588.trimOffspring", {"start": v(958.96, 1372.5) * mm, "end": v(1286.96, 1372.5) * mm});
            skLineSegment(sketch, "E589.trimOffspring", {"start": v(958.96, 1390.5) * mm, "end": v(1286.96, 1390.5) * mm});
            skLineSegment(sketch, "E590.trimOffspring", {"start": v(-871.4, 2249) * mm, "end": v(-871.4, 2199) * mm});
            skLineSegment(sketch, "E591.trimOffspring", {"start": v(-847.4, 2249) * mm, "end": v(-847.4, 2199) * mm});
            skLineSegment(sketch, "E592.trimOffspring", {"start": v(-847.4, 2564.17) * mm, "end": v(-696.32, 2626) * mm});
            skLineSegment(sketch, "E593.trimOffspring", {"start": v(-871.4, 2565.16) * mm, "end": v(-851.19, 2573.43) * mm});
            skLineSegment(sketch, "E594", {"start": v(-588.04, 2636) * mm, "end": v(-588.04, 2249) * mm});
            skLineSegment(sketch, "E595", {"start": v(-564.04, 2636) * mm, "end": v(-564.04, 2249) * mm});
            skLineSegment(sketch, "E596", {"start": v(1.96, 2249) * mm, "end": v(1.96, 2636) * mm});
            skLineSegment(sketch, "E597", {"start": v(25.96, 2636) * mm, "end": v(25.96, 2249) * mm});
            skLineSegment(sketch, "E598", {"start": v(591.96, 2636) * mm, "end": v(591.96, 2249) * mm});
            skLineSegment(sketch, "E599", {"start": v(615.93, 2249) * mm, "end": v(615.93, 2636) * mm});
            skLineSegment(sketch, "E600", {"start": v(941.96, 2636) * mm, "end": v(941.96, 2249) * mm});
            skLineSegment(sketch, "E601", {"start": v(965.96, 2626) * mm, "end": v(965.96, 2249) * mm});
            skLineSegment(sketch, "E602", {"start": v(1279.96, 2626) * mm, "end": v(1279.96, 2249) * mm});
            skLineSegment(sketch, "E603.trimOffspring", {"start": v(-571.04, 741) * mm, "end": v(-1659.04, 741) * mm});
            skLineSegment(sketch, "E604.trimOffspring", {"start": v(-588.04, 759) * mm, "end": v(-1659.04, 759) * mm});
            skLineSegment(sketch, "E605.0", {"start": v(-1395.53, 1515.2) * mm, "end": v(-1371.53, 1515.2) * mm});
            skLineSegment(sketch, "E606.trimOffspring", {"start": v(-871.4, 1515.2) * mm, "end": v(-847.4, 1515.2) * mm});
            skLineSegment(sketch, "E607", {"start": v(-588.04, 1504.2) * mm, "end": v(-1652.04, 1504.2) * mm});
            skLineSegment(sketch, "E608.trimOffspring", {"start": v(1279.96, 526) * mm, "end": v(1279.96, 502) * mm});
            skLineSegment(sketch, "E609.trimOffspring", {"start": v(-1652.04, 2234.89) * mm, "end": v(-871.4, 2554.35) * mm});
            skLineSegment(sketch, "E610", {"start": v(327.96, 447.8) * mm, "end": v(327.96, -2.2) * mm});
            skLineSegment(sketch, "E611", {"start": v(727.96, 447.8) * mm, "end": v(727.96, -2.2) * mm});
            skLineSegment(sketch, "E612.trimOffspring", {"start": v(-624.04, 650) * mm, "end": v(-224.04, 650) * mm});
            skLineSegment(sketch, "E613.trimOffspring", {"start": v(-148.04, 650) * mm, "end": v(251.96, 650) * mm});
            skLineSegment(sketch, "E614.trimOffspring", {"start": v(327.96, 650) * mm, "end": v(727.96, 650) * mm});
            skLineSegment(sketch, "E615.trimOffspring", {"start": v(803.96, 650) * mm, "end": v(1203.96, 650) * mm});
            skLineSegment(sketch, "E616", {"start": v(8.96, 741) * mm, "end": v(18.96, 741) * mm});
            skLineSegment(sketch, "E617", {"start": v(1279.96, 550) * mm, "end": v(1279.96, 526) * mm});
            skLineSegment(sketch, "E618.0", {"start": v(965.96, 752) * mm, "end": v(941.96, 752) * mm});
            skLineSegment(sketch, "E619.trimOffspring", {"start": v(941.96, 759) * mm, "end": v(615.96, 759) * mm});
            skLineSegment(sketch, "E620.trimOffspring", {"start": v(591.96, 759) * mm, "end": v(25.96, 759) * mm});
            skLineSegment(sketch, "E621.trimOffspring", {"start": v(615.96, 752) * mm, "end": v(591.96, 752) * mm});
            skLineSegment(sketch, "E622.trimOffspring", {"start": v(-564.04, 752) * mm, "end": v(-588.04, 752) * mm});
            skLineSegment(sketch, "E623.trimOffspring", {"start": v(25.96, 752) * mm, "end": v(1.96, 752) * mm});
            skLineSegment(sketch, "E624.trimOffspring", {"start": v(1286.96, 759) * mm, "end": v(1286.96, 741) * mm});
            skLineSegment(sketch, "E625.trimOffspring", {"start": v(1279.96, 741) * mm, "end": v(1279.96, 550) * mm});
            skLineSegment(sketch, "E626", {"start": v(-701.04, 2650) * mm, "end": v(-696.32, 2626) * mm});
            skLineSegment(sketch, "E627", {"start": v(-1659.04, 2199) * mm, "end": v(-1659.04, 2181) * mm});
            skLineSegment(sketch, "E628", {"start": v(-1659.04, 2181) * mm, "end": v(-1652.04, 2181) * mm});
            skLineSegment(sketch, "E629.0", {"start": v(-1659.04, 2181) * mm, "end": v(-1395.53, 2181) * mm});
            skLineSegment(sketch, "E630.0", {"start": v(-1659.04, 2199) * mm, "end": v(-1377.37, 2199) * mm});
            skLineSegment(sketch, "E631", {"start": v(1286.96, 2199) * mm, "end": v(1286.96, 2181) * mm});
            skLineSegment(sketch, "E632", {"start": v(958.96, 2199) * mm, "end": v(958.96, 2181) * mm});
            skLineSegment(sketch, "E633", {"start": v(948.96, 2199) * mm, "end": v(948.96, 2181) * mm});
            skLineSegment(sketch, "E634.trimOffspring", {"start": v(958.96, 2199) * mm, "end": v(1286.96, 2199) * mm});
            skLineSegment(sketch, "E635.trimOffspring", {"start": v(958.96, 2181) * mm, "end": v(1286.96, 2181) * mm});
            skLineSegment(sketch, "E636.trimOffspring", {"start": v(608.93, 2199) * mm, "end": v(608.93, 2181) * mm});
            skLineSegment(sketch, "E637.trimOffspring", {"start": v(608.93, 2199) * mm, "end": v(948.96, 2199) * mm});
            skLineSegment(sketch, "E638.trimOffspring", {"start": v(608.93, 2181) * mm, "end": v(948.96, 2181) * mm});
            skLineSegment(sketch, "E639.trimOffspring", {"start": v(598.96, 2181) * mm, "end": v(598.96, 2199) * mm});
            skLineSegment(sketch, "E640", {"start": v(18.96, 2199) * mm, "end": v(18.96, 2181) * mm});
            skLineSegment(sketch, "E641", {"start": v(8.96, 2199) * mm, "end": v(8.96, 2181) * mm});
            skLineSegment(sketch, "E642.trimOffspring", {"start": v(18.96, 2199) * mm, "end": v(598.96, 2199) * mm});
            skLineSegment(sketch, "E643.trimOffspring", {"start": v(18.96, 2181) * mm, "end": v(598.96, 2181) * mm});
            skLineSegment(sketch, "E644.trimOffspring", {"start": v(-1377.37, 2199) * mm, "end": v(-864.4, 2199) * mm});
            skLineSegment(sketch, "E645.trimOffspring", {"start": v(-1371.53, 2181) * mm, "end": v(-864.4, 2181) * mm});
            skLineSegment(sketch, "E646.trimOffspring", {"start": v(-854, 2199) * mm, "end": v(-581.04, 2199) * mm});
            skLineSegment(sketch, "E647.trimOffspring", {"start": v(-854, 2181) * mm, "end": v(-581.04, 2181) * mm});
            skLineSegment(sketch, "E648.trimOffspring", {"start": v(-864.4, 2199) * mm, "end": v(-864.4, 2181) * mm});
            skLineSegment(sketch, "E649.trimOffspring", {"start": v(-854, 2181) * mm, "end": v(-854, 2199) * mm});
            skLineSegment(sketch, "E650", {"start": v(-571.04, 2199) * mm, "end": v(-571.04, 2181) * mm});
            skLineSegment(sketch, "E651.trimOffspring", {"start": v(-571.04, 2199) * mm, "end": v(8.96, 2199) * mm});
            skLineSegment(sketch, "E652.trimOffspring", {"start": v(-571.04, 2181) * mm, "end": v(8.96, 2181) * mm});
            skLineSegment(sketch, "E653.trimOffspring", {"start": v(-581.04, 2199) * mm, "end": v(-581.04, 2181) * mm});
            skLineSegment(sketch, "E654.trimOffspring", {"start": v(-1395.53, 2186) * mm, "end": v(-1371.53, 2186) * mm});
            skLineSegment(sketch, "E655.trimOffspring", {"start": v(-871.4, 2181) * mm, "end": v(-871.4, 1807) * mm});
            skLineSegment(sketch, "E656.trimOffspring", {"start": v(-847.4, 2181) * mm, "end": v(-847.4, 1807) * mm});
            skLineSegment(sketch, "E657.trimOffspring", {"start": v(-588.04, 2199) * mm, "end": v(-588.04, 2249) * mm});
            skLineSegment(sketch, "E658.trimOffspring", {"start": v(-564.04, 2199) * mm, "end": v(-564.04, 2249) * mm});
            skLineSegment(sketch, "E659.trimOffspring", {"start": v(1.96, 2199) * mm, "end": v(1.96, 2249) * mm});
            skLineSegment(sketch, "E660.trimOffspring", {"start": v(25.96, 2199) * mm, "end": v(25.96, 2249) * mm});
            skLineSegment(sketch, "E661.trimOffspring", {"start": v(591.96, 2199) * mm, "end": v(591.96, 2249) * mm});
            skLineSegment(sketch, "E662.trimOffspring", {"start": v(615.93, 2199) * mm, "end": v(615.93, 2249) * mm});
            skLineSegment(sketch, "E663.trimOffspring", {"start": v(941.96, 2181) * mm, "end": v(941.96, 1807) * mm});
            skLineSegment(sketch, "E664.trimOffspring", {"start": v(965.96, 2181) * mm, "end": v(965.96, 1807) * mm});
            skLineSegment(sketch, "E665.trimOffspring", {"start": v(1279.96, 2181) * mm, "end": v(1279.96, 1807) * mm});
            skLineSegment(sketch, "E666", {"start": v(-1676.04, 2251) * mm, "end": v(-1652.04, 2234.89) * mm});
            skLineSegment(sketch, "E667.trimOffspring", {"start": v(-1652.04, 2199) * mm, "end": v(-1652.04, 2234.89) * mm});
            skLineSegment(sketch, "E668", {"start": v(-864.4, 1807) * mm, "end": v(-864.4, 1783) * mm});
            skLineSegment(sketch, "E669", {"start": v(-847.4, 2564.17) * mm, "end": v(-851.19, 2573.43) * mm});
            skSolve(sketch);
        }
        {
            var Q0;
            {var subQ6=sQuery(id+"F3.wireOp",EDGE,"a6bb4a7d-90e6-44ad-8111-e173b3c4cc0b");Q0=makeQuery(id+"F3.imprint","IMPRINT",FACE,{"disambiguationData":[TD([[makeQuery(id+"F3.imprint","IMPRINT",EDGE,{"derivedFrom":subQ6}),-1.0]])]});}
            var Q1;
            Q1=makeQuery(id+"F3.imprint","IMPRINT",FACE,{"disambiguationData":[TD([[makeQuery(id+"F3.imprint","IMPRINT",EDGE,{"derivedFrom":sQuery(id+"F3.wireOp",EDGE,"E446")}),-1.0]])]});
            extrude(context, id + "F4", {"entities" : qUnion([Q0, Q1]), "depth" : 400 * mm, "offsetDistance" : 25 * mm});
        }
        {
            var Q0;
            {var subQ1=sQuery(id+"F2.wireOp",EDGE,"E235.0");Q0=makeQuery(id+"F2.imprint","IMPRINT",FACE,{"disambiguationData":[TD([[makeQuery(id+"F2.imprint","IMPRINT",EDGE,{"derivedFrom":subQ1}),1.0]])]});}
            var Q1;
            {var subQ13=sQuery(id+"F2.wireOp",EDGE,"5834afbf-c060-4856-86f9-8fd6da38f6a5.trimOffspring");Q1=makeQuery(id+"F2.imprint","IMPRINT",FACE,{"disambiguationData":[TD([[makeQuery(id+"F2.imprint","IMPRINT",EDGE,{"derivedFrom":subQ13}),1.0]])]});}
            var Q2;
            {var subQ2=sQuery(id+"F2.wireOp",EDGE,"E355.trimOffspring");Q2=makeQuery(id+"F2.imprint","IMPRINT",FACE,{"disambiguationData":[TD([[makeQuery(id+"F2.imprint","IMPRINT",EDGE,{"derivedFrom":subQ2}),-1.0]])]});}
            var Q3;
            {var subQ0=sQuery(id+"F2.wireOp",EDGE,"E352.trimOffspring");Q3=makeQuery(id+"F2.imprint","IMPRINT",FACE,{"disambiguationData":[TD([[makeQuery(id+"F2.imprint","IMPRINT",EDGE,{"derivedFrom":subQ0}),1.0]])]});}
            var Q4;
            {var subQ0=sQuery(id+"F2.wireOp",EDGE,"E314.trimOffspring");Q4=makeQuery(id+"F2.imprint","IMPRINT",FACE,{"disambiguationData":[TD([[makeQuery(id+"F2.imprint","IMPRINT",EDGE,{"derivedFrom":subQ0}),1.0]])]});}
            var Q5;
            {var subQ4=sQuery(id+"F2.wireOp",EDGE,"E305.trimOffspring");Q5=makeQuery(id+"F2.imprint","IMPRINT",FACE,{"disambiguationData":[TD([[makeQuery(id+"F2.imprint","IMPRINT",EDGE,{"derivedFrom":subQ4}),-1.0]])]});}
            var Q6;
            {var subQ4=sQuery(id+"F2.wireOp",EDGE,"E292.trimOffspring");Q6=makeQuery(id+"F2.imprint","IMPRINT",FACE,{"disambiguationData":[TD([[makeQuery(id+"F2.imprint","IMPRINT",EDGE,{"derivedFrom":subQ4}),-1.0]])]});}
            var Q7;
            {var subQ2=sQuery(id+"F2.wireOp",EDGE,"E291");Q7=makeQuery(id+"F2.imprint","IMPRINT",FACE,{"disambiguationData":[TD([[makeQuery(id+"F2.imprint","IMPRINT",EDGE,{"derivedFrom":subQ2}),-1.0]])]});}
            var Q8;
            {var subQ3=sQuery(id+"F2.wireOp",EDGE,"E304");Q8=makeQuery(id+"F2.imprint","IMPRINT",FACE,{"disambiguationData":[TD([[makeQuery(id+"F2.imprint","IMPRINT",EDGE,{"derivedFrom":subQ3}),-1.0]])]});}
            var Q9;
            {var subQ0=sQuery(id+"F2.wireOp",EDGE,"E309");Q9=makeQuery(id+"F2.imprint","IMPRINT",FACE,{"disambiguationData":[TD([[makeQuery(id+"F2.imprint","IMPRINT",EDGE,{"derivedFrom":subQ0}),1.0]])]});}
            var Q10;
            Q10=makeQuery(id+"F2.imprint","IMPRINT",FACE,{"disambiguationData":[TD([[makeQuery(id+"F2.imprint","IMPRINT",EDGE,{"derivedFrom":sQuery(id+"F2.wireOp",EDGE,"E264.0")}),-1.0]])]});
            var Q11;
            {var subQ3=sQuery(id+"F2.wireOp",EDGE,"84c29c2e-81eb-4c6d-877f-103eb5f7c7c5.trimOffspring");Q11=makeQuery(id+"F2.imprint","IMPRINT",FACE,{"disambiguationData":[TD([[makeQuery(id+"F2.imprint","IMPRINT",EDGE,{"derivedFrom":subQ3}),-1.0]])]});}
            var Q12;
            {var subQ1=sQuery(id+"F2.wireOp",EDGE,"E324.trimOffspring");Q12=makeQuery(id+"F2.imprint","IMPRINT",FACE,{"disambiguationData":[TD([[makeQuery(id+"F2.imprint","IMPRINT",EDGE,{"derivedFrom":subQ1}),-1.0]])]});}
            var Q13;
            {var subQ4=sQuery(id+"F2.wireOp",EDGE,"E285");Q13=makeQuery(id+"F2.imprint","IMPRINT",FACE,{"disambiguationData":[TD([[makeQuery(id+"F2.imprint","IMPRINT",EDGE,{"derivedFrom":subQ4}),1.0]])]});}
            var Q14;
            {var subQ6=sQuery(id+"F2.wireOp",EDGE,"E397");Q14=makeQuery(id+"F2.imprint","IMPRINT",FACE,{"disambiguationData":[TD([[makeQuery(id+"F2.imprint","IMPRINT",EDGE,{"derivedFrom":subQ6}),1.0]])]});}
            var Q15;
            {var subQ0=sQuery(id+"F2.wireOp",EDGE,"5d32728e-9b4f-4f90-8e41-ef28475b609c.trimOffspring");Q15=makeQuery(id+"F2.imprint","IMPRINT",FACE,{"disambiguationData":[TD([[makeQuery(id+"F2.imprint","IMPRINT",EDGE,{"derivedFrom":subQ0}),-1.0]])]});}
            var Q16;
            {var subQ4=sQuery(id+"F2.wireOp",EDGE,"E411");Q16=makeQuery(id+"F2.imprint","IMPRINT",FACE,{"disambiguationData":[TD([[makeQuery(id+"F2.imprint","IMPRINT",EDGE,{"derivedFrom":subQ4}),-1.0]])]});}
            var Q17;
            {var subQ4=sQuery(id+"F2.wireOp",EDGE,"E409.trimOffspring");Q17=makeQuery(id+"F2.imprint","IMPRINT",FACE,{"disambiguationData":[TD([[makeQuery(id+"F2.imprint","IMPRINT",EDGE,{"derivedFrom":subQ4}),1.0]])]});}
            var Q18;
            {var subQ4=sQuery(id+"F2.wireOp",EDGE,"E403");Q18=makeQuery(id+"F2.imprint","IMPRINT",FACE,{"disambiguationData":[TD([[makeQuery(id+"F2.imprint","IMPRINT",EDGE,{"derivedFrom":subQ4}),-1.0]])]});}
            var Q19;
            {var subQ4=sQuery(id+"F2.wireOp",EDGE,"E401");Q19=makeQuery(id+"F2.imprint","IMPRINT",FACE,{"disambiguationData":[TD([[makeQuery(id+"F2.imprint","IMPRINT",EDGE,{"derivedFrom":subQ4}),-1.0]])]});}
            var Q20;
            {var subQ14=sQuery(id+"F2.wireOp",EDGE,"E316.trimOffspring");Q20=makeQuery(id+"F2.imprint","IMPRINT",FACE,{"disambiguationData":[TD([[makeQuery(id+"F2.imprint","IMPRINT",EDGE,{"derivedFrom":subQ14}),1.0]])]});}
            var Q21;
            {var subQ3=sQuery(id+"F2.wireOp",EDGE,"E422.trimOffspring");Q21=makeQuery(id+"F2.imprint","IMPRINT",FACE,{"disambiguationData":[TD([[makeQuery(id+"F2.imprint","IMPRINT",EDGE,{"derivedFrom":subQ3}),-1.0]])]});}
            var Q22;
            {var subQ2=sQuery(id+"F2.wireOp",EDGE,"E335.trimOffspring");Q22=makeQuery(id+"F2.imprint","IMPRINT",FACE,{"disambiguationData":[TD([[makeQuery(id+"F2.imprint","IMPRINT",EDGE,{"derivedFrom":subQ2}),-1.0]])]});}
            extrude(context, id + "F5", {"entities" : qUnion([Q0, Q1, Q2, Q3, Q4, Q5, Q6, Q7, Q8, Q9, Q10, Q11, Q12, Q13, Q14, Q15, Q16, Q17, Q18, Q19, Q20, Q21, Q22]), "depth" : 400 * mm, "offsetDistance" : 25 * mm});
        }
    });
